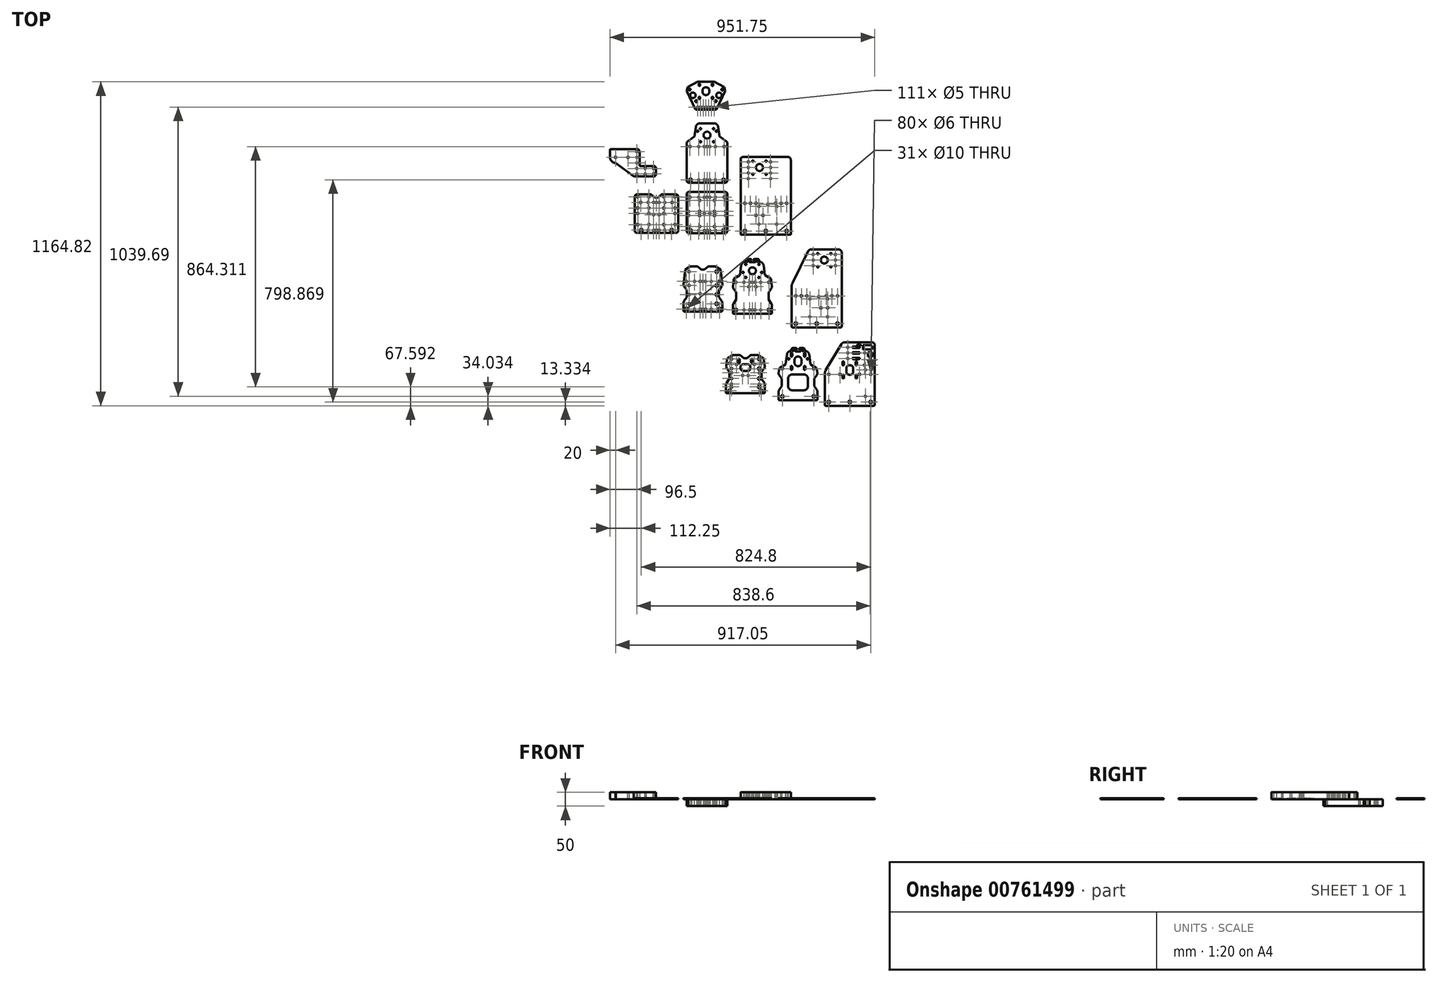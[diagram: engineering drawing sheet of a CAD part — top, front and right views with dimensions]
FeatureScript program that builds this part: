
annotation { "Feature Type Name" : "Feature", "Feature Type Description" : "" }
export const myFeature = defineFeature(function(context is Context, id is Id, definition is map)
    precondition{}
    {
        {
            var Q0;
            Q0=qCreatedBy(makeId("Top.planeOp"),FACE);
            var sketch = newSketch(context, id + "F0", { "sketchPlane" : qUnion([Q0])});
            skLineSegment(sketch, "E0", {"start": v(-86.67, -113.77) * mm, "end": v(86.64, -113.77) * mm});
            skLineSegment(sketch, "E1", {"start": v(-90, -1.46) * mm, "end": v(-90, -110.4) * mm});
            skLineSegment(sketch, "E2", {"start": v(-30.03, 107.94) * mm, "end": v(-86.68, 13.65) * mm});
            skLineSegment(sketch, "E3", {"start": v(-26.11, -13.56) * mm, "end": v(-26.11, -4.56) * mm});
            skLineSegment(sketch, "E4", {"start": v(-26.11, 33.58) * mm, "end": v(-26.11, 42.58) * mm});
            skLineSegment(sketch, "E5", {"start": v(-21.03, 42.58) * mm, "end": v(-21.03, 33.58) * mm});
            skLineSegment(sketch, "E6", {"start": v(-21.03, -4.56) * mm, "end": v(-21.03, -13.56) * mm});
            skLineSegment(sketch, "E7", {"start": v(-12.5, 9.51) * mm, "end": v(-12.5, 19.51) * mm});
            skLineSegment(sketch, "E8", {"start": v(12.5, 19.51) * mm, "end": v(12.5, 9.51) * mm});
            skLineSegment(sketch, "E9", {"start": v(21.03, -13.56) * mm, "end": v(21.03, -4.56) * mm});
            skLineSegment(sketch, "E10", {"start": v(21.03, 33.58) * mm, "end": v(21.03, 42.58) * mm});
            skLineSegment(sketch, "E11", {"start": v(26.1, 42.58) * mm, "end": v(26.1, 33.58) * mm});
            skLineSegment(sketch, "E12", {"start": v(26.1, -4.56) * mm, "end": v(26.1, -13.56) * mm});
            skLineSegment(sketch, "E13", {"start": v(27.19, 103.2) * mm, "end": v(27.19, 105.32) * mm});
            skLineSegment(sketch, "E14", {"start": v(76.37, 62.2) * mm, "end": v(75.8, 61.48) * mm});
            skLineSegment(sketch, "E15", {"start": v(39.19, 105.32) * mm, "end": v(39.19, 103.2) * mm});
            skLineSegment(sketch, "E16", {"start": v(47, 91.4) * mm, "end": v(47, 101.1) * mm});
            skLineSegment(sketch, "E17", {"start": v(33.19, 53.67) * mm, "end": v(12.19, 53.67) * mm});
            skLineSegment(sketch, "E18", {"start": v(12.19, 58.67) * mm, "end": v(33.19, 58.67) * mm});
            skLineSegment(sketch, "E19", {"start": v(65.8, 64.35) * mm, "end": v(65.8, 76.68) * mm});
            skLineSegment(sketch, "E20", {"start": v(78.84, 62.2) * mm, "end": v(76.37, 62.2) * mm});
            skLineSegment(sketch, "E21", {"start": v(69.93, 62.7) * mm, "end": v(67.46, 62.7) * mm});
            skLineSegment(sketch, "E22", {"start": v(33.19, 73.67) * mm, "end": v(12.19, 73.67) * mm});
            skLineSegment(sketch, "E23", {"start": v(67.46, 78.34) * mm, "end": v(78.84, 78.34) * mm});
            skLineSegment(sketch, "E24", {"start": v(80.5, 97.88) * mm, "end": v(80.5, 91.4) * mm});
            skLineSegment(sketch, "E25", {"start": v(80.5, 76.68) * mm, "end": v(80.5, 63.85) * mm});
            skLineSegment(sketch, "E26", {"start": v(12.19, 78.67) * mm, "end": v(33.19, 78.67) * mm});
            skLineSegment(sketch, "E27", {"start": v(77.36, 88.26) * mm, "end": v(50.14, 88.26) * mm});
            skLineSegment(sketch, "E28", {"start": v(90, -110.4) * mm, "end": v(90, 104.05) * mm});
            skLineSegment(sketch, "E29", {"start": v(33.19, 93.67) * mm, "end": v(12.19, 93.67) * mm});
            skLineSegment(sketch, "E30", {"start": v(70.9, 61.48) * mm, "end": v(69.93, 62.7) * mm});
            skLineSegment(sketch, "E31", {"start": v(12.19, 98.67) * mm, "end": v(33.19, 98.67) * mm});
            skLineSegment(sketch, "E32", {"start": v(37.75, 101.76) * mm, "end": v(28.63, 101.76) * mm});
            skLineSegment(sketch, "E33", {"start": v(50.14, 104.23) * mm, "end": v(74.15, 104.23) * mm});
            skLineSegment(sketch, "E34", {"start": v(28.63, 106.76) * mm, "end": v(37.75, 106.76) * mm});
            skLineSegment(sketch, "E35", {"start": v(80.33, 113.73) * mm, "end": v(-18.85, 113.73) * mm});
            skCircle(sketch, "E36", {"center": v(-75.3, -100.44) * mm, "radius": 5 * mm});
            skArc(sketch, "E37", {"start": v(-90, -110.4) * mm, "mid": v(-89.03, -112.77) * mm, "end": v(-86.67, -113.77) * mm});
            skArc(sketch, "E38", {"start": v(-26.11, -13.56) * mm, "mid": v(-23.57, -16.1) * mm, "end": v(-21.03, -13.56) * mm});
            skArc(sketch, "E39", {"start": v(-21.03, -4.56) * mm, "mid": v(-23.57, -2.02) * mm, "end": v(-26.11, -4.56) * mm});
            skArc(sketch, "E40", {"start": v(-86.68, 13.65) * mm, "mid": v(-89.16, 6.28) * mm, "end": v(-90, -1.46) * mm});
            skArc(sketch, "E41", {"start": v(-18.85, 113.73) * mm, "mid": v(-25.26, 112.42) * mm, "end": v(-30.03, 107.94) * mm});
            skArc(sketch, "E42", {"start": v(-21.03, 42.58) * mm, "mid": v(-23.57, 45.12) * mm, "end": v(-26.11, 42.58) * mm});
            skArc(sketch, "E43", {"start": v(-26.11, 33.58) * mm, "mid": v(-23.57, 31.04) * mm, "end": v(-21.03, 33.58) * mm});
            skCircle(sketch, "E44", {"center": v(-7.31, 96.17) * mm, "radius": 2.5 * mm});
            skCircle(sketch, "E45", {"center": v(-7.31, 76.17) * mm, "radius": 2.5 * mm});
            skCircle(sketch, "E46", {"center": v(-7.31, 56.17) * mm, "radius": 2.5 * mm});
            skCircle(sketch, "E47", {"center": v(-35.3, -0.74) * mm, "radius": 3 * mm});
            skCircle(sketch, "E48", {"center": v(-75.3, -0.74) * mm, "radius": 3 * mm});
            skCircle(sketch, "E49", {"center": v(75.3, -100.44) * mm, "radius": 5 * mm});
            skCircle(sketch, "E50", {"center": v(0, -100.44) * mm, "radius": 5 * mm});
            skArc(sketch, "E51", {"start": v(86.64, -113.77) * mm, "mid": v(89.02, -112.78) * mm, "end": v(90, -110.4) * mm});
            skArc(sketch, "E52", {"start": v(21.03, -13.56) * mm, "mid": v(23.57, -16.1) * mm, "end": v(26.1, -13.56) * mm});
            skArc(sketch, "E53", {"start": v(26.1, -4.56) * mm, "mid": v(23.57, -2.02) * mm, "end": v(21.03, -4.56) * mm});
            skCircle(sketch, "E54", {"center": v(56.34, -79.74) * mm, "radius": 2.5 * mm});
            skArc(sketch, "E55", {"start": v(-12.5, 9.51) * mm, "mid": v(0, -2.99) * mm, "end": v(12.5, 9.51) * mm});
            skArc(sketch, "E56", {"start": v(12.5, 19.51) * mm, "mid": v(0, 32.01) * mm, "end": v(-12.5, 19.51) * mm});
            skArc(sketch, "E57", {"start": v(90, 104.05) * mm, "mid": v(87.17, 110.9) * mm, "end": v(80.33, 113.73) * mm});
            skArc(sketch, "E58", {"start": v(80.5, 97.88) * mm, "mid": v(78.64, 102.37) * mm, "end": v(74.15, 104.23) * mm});
            skArc(sketch, "E59", {"start": v(77.36, 88.26) * mm, "mid": v(79.58, 89.18) * mm, "end": v(80.5, 91.4) * mm});
            skArc(sketch, "E60", {"start": v(47, 91.4) * mm, "mid": v(47.92, 89.18) * mm, "end": v(50.14, 88.26) * mm});
            skArc(sketch, "E61", {"start": v(50.14, 104.23) * mm, "mid": v(47.92, 103.31) * mm, "end": v(47, 101.1) * mm});
            skArc(sketch, "E62", {"start": v(21.03, 33.58) * mm, "mid": v(23.57, 31.04) * mm, "end": v(26.1, 33.58) * mm});
            skArc(sketch, "E63", {"start": v(26.1, 42.58) * mm, "mid": v(23.57, 45.12) * mm, "end": v(21.03, 42.58) * mm});
            skArc(sketch, "E64", {"start": v(33.19, 93.67) * mm, "mid": v(35.69, 96.17) * mm, "end": v(33.19, 98.67) * mm});
            skArc(sketch, "E65", {"start": v(12.19, 98.67) * mm, "mid": v(9.69, 96.17) * mm, "end": v(12.19, 93.67) * mm});
            skArc(sketch, "E66", {"start": v(33.19, 73.67) * mm, "mid": v(35.69, 76.17) * mm, "end": v(33.19, 78.67) * mm});
            skArc(sketch, "E67", {"start": v(12.19, 78.67) * mm, "mid": v(9.69, 76.17) * mm, "end": v(12.19, 73.67) * mm});
            skArc(sketch, "E68", {"start": v(33.19, 53.67) * mm, "mid": v(35.69, 56.17) * mm, "end": v(33.19, 58.67) * mm});
            skArc(sketch, "E69", {"start": v(12.19, 58.67) * mm, "mid": v(9.69, 56.17) * mm, "end": v(12.19, 53.67) * mm});
            skCircle(sketch, "E70", {"center": v(53.69, 76.17) * mm, "radius": 2.5 * mm});
            skCircle(sketch, "E71", {"center": v(73.35, 52.21) * mm, "radius": 2.5 * mm});
            skCircle(sketch, "E72", {"center": v(73.35, 32.21) * mm, "radius": 2.5 * mm});
            skCircle(sketch, "E73", {"center": v(52.85, 32.21) * mm, "radius": 2.5 * mm});
            skCircle(sketch, "E74", {"center": v(56.34, 15.26) * mm, "radius": 2.5 * mm});
            skCircle(sketch, "E75", {"center": v(75.3, -0.74) * mm, "radius": 3 * mm});
            skCircle(sketch, "E76", {"center": v(35.3, -0.74) * mm, "radius": 3 * mm});
            skArc(sketch, "E77", {"start": v(80.5, 76.68) * mm, "mid": v(80.01, 77.86) * mm, "end": v(78.84, 78.34) * mm});
            skArc(sketch, "E78", {"start": v(78.84, 62.2) * mm, "mid": v(80.01, 62.68) * mm, "end": v(80.5, 63.85) * mm});
            skArc(sketch, "E79", {"start": v(65.8, 64.35) * mm, "mid": v(66.29, 63.18) * mm, "end": v(67.46, 62.7) * mm});
            skArc(sketch, "E80", {"start": v(67.46, 78.34) * mm, "mid": v(66.29, 77.86) * mm, "end": v(65.8, 76.68) * mm});
            skArc(sketch, "E81", {"start": v(39.19, 105.32) * mm, "mid": v(38.77, 106.34) * mm, "end": v(37.75, 106.76) * mm});
            skArc(sketch, "E82", {"start": v(37.75, 101.76) * mm, "mid": v(38.77, 102.19) * mm, "end": v(39.19, 103.2) * mm});
            skArc(sketch, "E83", {"start": v(27.19, 103.2) * mm, "mid": v(27.61, 102.19) * mm, "end": v(28.63, 101.76) * mm});
            skArc(sketch, "E84", {"start": v(28.63, 106.76) * mm, "mid": v(27.61, 106.34) * mm, "end": v(27.19, 105.32) * mm});
            skEllipticalArc(sketch, "E85", {});
            const initialGuessF0  = {"E85": [0.07334998479999985, 0.06148353816120338, 1, 0, 0.0024529870000000007, 0.0024529870000000007, 3.141592307179585, 0]};
            skSetInitialGuess(sketch, initialGuessF0);
            skSolve(sketch);
        }
        {
            var Q0;
            Q0 = qSketchRegion(id + "F0", true);
            extrude(context, id + "F1", {"entities" : qUnion([Q0]), "depth" : 3 * mm, "offsetDistance" : 25 * mm});
        }
        {
            var Q0;
            Q0=qCreatedBy(makeId("Top.planeOp"),FACE);
            var sketch = newSketch(context, id + "F2", { "sketchPlane" : qUnion([Q0])});
            skLineSegment(sketch, "E86", {"start": v(-252.64, -93.7) * mm, "end": v(-119.36, -93.7) * mm});
            skLineSegment(sketch, "E87", {"start": v(-256, -62.59) * mm, "end": v(-256, -90.34) * mm});
            skLineSegment(sketch, "E88", {"start": v(-255.52, 3.6) * mm, "end": v(-253.3, 19.33) * mm});
            skLineSegment(sketch, "E89", {"start": v(-253.3, 19.33) * mm, "end": v(-253, 20.67) * mm});
            skLineSegment(sketch, "E90", {"start": v(-253, 20.67) * mm, "end": v(-252.46, 21.77) * mm});
            skLineSegment(sketch, "E91", {"start": v(-252.46, 21.77) * mm, "end": v(-251.76, 22.64) * mm});
            skLineSegment(sketch, "E92", {"start": v(-251.76, 22.64) * mm, "end": v(-250.88, 23.32) * mm});
            skLineSegment(sketch, "E93", {"start": v(-256, -62.59) * mm, "end": v(-255.87, -61.2) * mm});
            skLineSegment(sketch, "E94", {"start": v(-255.87, -61.2) * mm, "end": v(-255.45, -59.71) * mm});
            skLineSegment(sketch, "E95", {"start": v(-255.45, -59.71) * mm, "end": v(-254.73, -58.15) * mm});
            skLineSegment(sketch, "E96", {"start": v(-254.73, -58.15) * mm, "end": v(-253.73, -56.54) * mm});
            skLineSegment(sketch, "E97", {"start": v(-182.5, 90.85) * mm, "end": v(-180.18, 93.05) * mm});
            skLineSegment(sketch, "E98", {"start": v(-205.8, -58.65) * mm, "end": v(-166.2, -58.65) * mm});
            skLineSegment(sketch, "E99", {"start": v(-244.43, -16.42) * mm, "end": v(-252.79, -4.43) * mm});
            skLineSegment(sketch, "E100", {"start": v(-252.79, -4.43) * mm, "end": v(-253.92, -2.65) * mm});
            skLineSegment(sketch, "E101", {"start": v(-253.92, -2.65) * mm, "end": v(-254.76, -0.94) * mm});
            skLineSegment(sketch, "E102", {"start": v(-254.76, -0.94) * mm, "end": v(-255.32, 0.7) * mm});
            skLineSegment(sketch, "E103", {"start": v(-255.32, 0.7) * mm, "end": v(-255.56, 2.22) * mm});
            skLineSegment(sketch, "E104", {"start": v(-255.56, 2.22) * mm, "end": v(-255.52, 3.6) * mm});
            skLineSegment(sketch, "E105", {"start": v(-244, -41.83) * mm, "end": v(-244, -17.76) * mm});
            skLineSegment(sketch, "E106", {"start": v(-230.92, 36.33) * mm, "end": v(-226.1, 70.65) * mm});
            skLineSegment(sketch, "E107", {"start": v(-211.35, 84.55) * mm, "end": v(-210.83, 86.12) * mm});
            skLineSegment(sketch, "E108", {"start": v(-250.88, 23.32) * mm, "end": v(-232.03, 34.64) * mm});
            skLineSegment(sketch, "E109", {"start": v(-221.85, -17) * mm, "end": v(-221.85, -42.6) * mm});
            skLineSegment(sketch, "E110", {"start": v(-212.11, 73.84) * mm, "end": v(-212.11, 64.84) * mm});
            skLineSegment(sketch, "E111", {"start": v(-212.11, 26.7) * mm, "end": v(-212.11, 17.7) * mm});
            skLineSegment(sketch, "E112", {"start": v(-207.03, 17.7) * mm, "end": v(-207.03, 26.7) * mm});
            skLineSegment(sketch, "E113", {"start": v(-207.03, 64.84) * mm, "end": v(-207.03, 73.84) * mm});
            skLineSegment(sketch, "E114", {"start": v(-253.73, -56.54) * mm, "end": v(-244.43, -43.18) * mm});
            skLineSegment(sketch, "E115", {"start": v(-198.5, 50.77) * mm, "end": v(-198.5, 40.77) * mm});
            skLineSegment(sketch, "E116", {"start": v(-166.2, -0.95) * mm, "end": v(-205.8, -0.95) * mm});
            skLineSegment(sketch, "E117", {"start": v(-173.5, 40.77) * mm, "end": v(-173.5, 50.77) * mm});
            skLineSegment(sketch, "E118", {"start": v(-164.97, 73.84) * mm, "end": v(-164.97, 64.84) * mm});
            skLineSegment(sketch, "E119", {"start": v(-164.97, 26.7) * mm, "end": v(-164.97, 17.7) * mm});
            skLineSegment(sketch, "E120", {"start": v(-127.57, -43.17) * mm, "end": v(-118.27, -56.54) * mm});
            skLineSegment(sketch, "E121", {"start": v(-159.9, 17.7) * mm, "end": v(-159.9, 26.7) * mm});
            skLineSegment(sketch, "E122", {"start": v(-159.9, 64.84) * mm, "end": v(-159.9, 73.84) * mm});
            skLineSegment(sketch, "E123", {"start": v(-150.15, -42.6) * mm, "end": v(-150.15, -17) * mm});
            skLineSegment(sketch, "E124", {"start": v(-139.97, 34.64) * mm, "end": v(-121.12, 23.32) * mm});
            skLineSegment(sketch, "E125", {"start": v(-161.17, 86.12) * mm, "end": v(-160.65, 84.55) * mm});
            skLineSegment(sketch, "E126", {"start": v(-145.9, 70.65) * mm, "end": v(-141.08, 36.33) * mm});
            skLineSegment(sketch, "E127", {"start": v(-128, -17.76) * mm, "end": v(-128, -41.83) * mm});
            skLineSegment(sketch, "E128", {"start": v(-119.22, -4.43) * mm, "end": v(-127.57, -16.42) * mm});
            skLineSegment(sketch, "E129", {"start": v(-121.12, 23.32) * mm, "end": v(-120.22, 22.62) * mm});
            skLineSegment(sketch, "E130", {"start": v(-120.22, 22.62) * mm, "end": v(-119.51, 21.74) * mm});
            skLineSegment(sketch, "E131", {"start": v(-119.51, 21.74) * mm, "end": v(-119, 20.65) * mm});
            skLineSegment(sketch, "E132", {"start": v(-119, 20.65) * mm, "end": v(-118.7, 19.33) * mm});
            skLineSegment(sketch, "E133", {"start": v(-191.82, 93.05) * mm, "end": v(-189.5, 90.85) * mm});
            skLineSegment(sketch, "E134", {"start": v(-116, -62.59) * mm, "end": v(-116.13, -61.2) * mm});
            skLineSegment(sketch, "E135", {"start": v(-116.13, -61.2) * mm, "end": v(-116.55, -59.71) * mm});
            skLineSegment(sketch, "E136", {"start": v(-116.55, -59.71) * mm, "end": v(-117.27, -58.15) * mm});
            skLineSegment(sketch, "E137", {"start": v(-117.27, -58.15) * mm, "end": v(-118.27, -56.54) * mm});
            skLineSegment(sketch, "E138", {"start": v(-118.7, 19.33) * mm, "end": v(-116.48, 3.6) * mm});
            skLineSegment(sketch, "E139", {"start": v(-116.48, 3.6) * mm, "end": v(-116.43, 2.22) * mm});
            skLineSegment(sketch, "E140", {"start": v(-116.43, 2.22) * mm, "end": v(-116.68, 0.7) * mm});
            skLineSegment(sketch, "E141", {"start": v(-116.68, 0.7) * mm, "end": v(-117.24, -0.94) * mm});
            skLineSegment(sketch, "E142", {"start": v(-117.24, -0.94) * mm, "end": v(-118.09, -2.65) * mm});
            skLineSegment(sketch, "E143", {"start": v(-118.09, -2.65) * mm, "end": v(-119.22, -4.43) * mm});
            skLineSegment(sketch, "E144", {"start": v(-116, -90.34) * mm, "end": v(-116, -62.59) * mm});
            skLineSegment(sketch, "E145", {"start": v(-193.5, 81.5) * mm, "end": v(-178.5, 81.5) * mm});
            skLineSegment(sketch, "E146", {"start": v(-178.5, 89.5) * mm, "end": v(-181.15, 89.5) * mm});
            skLineSegment(sketch, "E147", {"start": v(-190.85, 89.5) * mm, "end": v(-193.5, 89.5) * mm});
            skLineSegment(sketch, "E148", {"start": v(-168.09, 93.7) * mm, "end": v(-178.56, 93.7) * mm});
            skLineSegment(sketch, "E149", {"start": v(-193.44, 93.7) * mm, "end": v(-203.91, 93.7) * mm});
            skArc(sketch, "E150", {"start": v(-205.8, -0.95) * mm, "mid": v(-217.15, -5.65) * mm, "end": v(-221.85, -17) * mm});
            skArc(sketch, "E151", {"start": v(-221.85, -42.6) * mm, "mid": v(-217.15, -53.95) * mm, "end": v(-205.8, -58.65) * mm});
            skCircle(sketch, "E152", {"center": v(-242.5, -80.18) * mm, "radius": 5 * mm});
            skArc(sketch, "E153", {"start": v(-256, -90.34) * mm, "mid": v(-255.02, -92.72) * mm, "end": v(-252.64, -93.7) * mm});
            skArc(sketch, "E154", {"start": v(-244, -17.76) * mm, "mid": v(-244.11, -17.06) * mm, "end": v(-244.43, -16.42) * mm});
            skArc(sketch, "E155", {"start": v(-244.43, -43.18) * mm, "mid": v(-244.11, -42.54) * mm, "end": v(-244, -41.83) * mm});
            skArc(sketch, "E156", {"start": v(-213.34, 82.95) * mm, "mid": v(-221.84, 79) * mm, "end": v(-226.1, 70.65) * mm});
            skArc(sketch, "E157", {"start": v(-203.91, 93.7) * mm, "mid": v(-208.37, 91.91) * mm, "end": v(-210.36, 87.54) * mm});
            skArc(sketch, "E158", {"start": v(-193.5, 89.5) * mm, "mid": v(-197.5, 85.5) * mm, "end": v(-193.5, 81.5) * mm});
            skCircle(sketch, "E159", {"center": v(-203.9, 85.5) * mm, "radius": 2.73 * mm});
            skCircle(sketch, "E160", {"center": v(-219.8, 54.95) * mm, "radius": 2.73 * mm});
            skArc(sketch, "E161", {"start": v(-207.03, 73.84) * mm, "mid": v(-209.57, 76.38) * mm, "end": v(-212.11, 73.84) * mm});
            skArc(sketch, "E162", {"start": v(-212.11, 64.84) * mm, "mid": v(-209.57, 62.3) * mm, "end": v(-207.03, 64.84) * mm});
            skArc(sketch, "E163", {"start": v(-207.03, 26.7) * mm, "mid": v(-209.57, 29.24) * mm, "end": v(-212.11, 26.7) * mm});
            skArc(sketch, "E164", {"start": v(-212.11, 17.7) * mm, "mid": v(-209.57, 15.16) * mm, "end": v(-207.03, 17.7) * mm});
            skCircle(sketch, "E165", {"center": v(-242.5, 19.52) * mm, "radius": 3 * mm});
            skArc(sketch, "E166", {"start": v(-232.03, 34.64) * mm, "mid": v(-231.29, 35.36) * mm, "end": v(-230.92, 36.33) * mm});
            skArc(sketch, "E167", {"start": v(-213.34, 82.95) * mm, "mid": v(-212.1, 83.46) * mm, "end": v(-211.35, 84.55) * mm});
            skArc(sketch, "E168", {"start": v(-191.82, 93.05) * mm, "mid": v(-192.57, 93.53) * mm, "end": v(-193.44, 93.7) * mm});
            skArc(sketch, "E169", {"start": v(-190.85, 89.5) * mm, "mid": v(-189.47, 89.47) * mm, "end": v(-189.5, 90.85) * mm});
            skArc(sketch, "E170", {"start": v(-210.83, 86.12) * mm, "mid": v(-210.12, 86.67) * mm, "end": v(-210.36, 87.54) * mm});
            skArc(sketch, "E171", {"start": v(-166.2, -58.65) * mm, "mid": v(-154.85, -53.95) * mm, "end": v(-150.15, -42.6) * mm});
            skArc(sketch, "E172", {"start": v(-150.15, -17) * mm, "mid": v(-154.85, -5.65) * mm, "end": v(-166.2, -0.95) * mm});
            skCircle(sketch, "E173", {"center": v(-129.5, -80.18) * mm, "radius": 5 * mm});
            skArc(sketch, "E174", {"start": v(-119.36, -93.7) * mm, "mid": v(-116.98, -92.72) * mm, "end": v(-116, -90.34) * mm});
            skArc(sketch, "E175", {"start": v(-127.57, -16.42) * mm, "mid": v(-127.88, -17.06) * mm, "end": v(-128, -17.76) * mm});
            skArc(sketch, "E176", {"start": v(-128, -41.83) * mm, "mid": v(-127.88, -42.54) * mm, "end": v(-127.57, -43.17) * mm});
            skArc(sketch, "E177", {"start": v(-145.9, 70.65) * mm, "mid": v(-150.16, 79) * mm, "end": v(-158.66, 82.95) * mm});
            skArc(sketch, "E178", {"start": v(-173.5, 50.77) * mm, "mid": v(-186, 63.27) * mm, "end": v(-198.5, 50.77) * mm});
            skArc(sketch, "E179", {"start": v(-198.5, 40.77) * mm, "mid": v(-186, 28.27) * mm, "end": v(-173.5, 40.77) * mm});
            skArc(sketch, "E180", {"start": v(-161.64, 87.54) * mm, "mid": v(-163.63, 91.91) * mm, "end": v(-168.09, 93.7) * mm});
            skArc(sketch, "E181", {"start": v(-178.5, 81.5) * mm, "mid": v(-174.5, 85.5) * mm, "end": v(-178.5, 89.5) * mm});
            skCircle(sketch, "E182", {"center": v(-168.1, 85.5) * mm, "radius": 2.73 * mm});
            skCircle(sketch, "E183", {"center": v(-152.2, 54.95) * mm, "radius": 2.73 * mm});
            skArc(sketch, "E184", {"start": v(-159.9, 73.84) * mm, "mid": v(-162.43, 76.38) * mm, "end": v(-164.97, 73.84) * mm});
            skArc(sketch, "E185", {"start": v(-164.97, 64.84) * mm, "mid": v(-162.43, 62.3) * mm, "end": v(-159.9, 64.84) * mm});
            skArc(sketch, "E186", {"start": v(-159.9, 26.7) * mm, "mid": v(-162.43, 29.24) * mm, "end": v(-164.97, 26.7) * mm});
            skArc(sketch, "E187", {"start": v(-164.97, 17.7) * mm, "mid": v(-162.43, 15.16) * mm, "end": v(-159.9, 17.7) * mm});
            skCircle(sketch, "E188", {"center": v(-129.5, 19.52) * mm, "radius": 3 * mm});
            skArc(sketch, "E189", {"start": v(-141.08, 36.33) * mm, "mid": v(-140.71, 35.36) * mm, "end": v(-139.97, 34.64) * mm});
            skArc(sketch, "E190", {"start": v(-160.65, 84.55) * mm, "mid": v(-159.9, 83.46) * mm, "end": v(-158.66, 82.95) * mm});
            skArc(sketch, "E191", {"start": v(-178.56, 93.7) * mm, "mid": v(-179.43, 93.53) * mm, "end": v(-180.18, 93.05) * mm});
            skArc(sketch, "E192", {"start": v(-182.5, 90.85) * mm, "mid": v(-182.53, 89.47) * mm, "end": v(-181.15, 89.5) * mm});
            skArc(sketch, "E193", {"start": v(-161.64, 87.54) * mm, "mid": v(-161.88, 86.67) * mm, "end": v(-161.17, 86.12) * mm});
            skSolve(sketch);
        }
        {
            var Q0;
            Q0=qCreatedBy(makeId("Top.planeOp"),FACE);
            var sketch = newSketch(context, id + "F3", { "sketchPlane" : qUnion([Q0])});
            skLineSegment(sketch, "E194", {"start": v(-438.59, 57.34) * mm, "end": v(-439.5, 56.65) * mm});
            skLineSegment(sketch, "E195", {"start": v(-439.5, 56.65) * mm, "end": v(-440.2, 55.76) * mm});
            skLineSegment(sketch, "E196", {"start": v(-440.2, 55.76) * mm, "end": v(-440.7, 54.68) * mm});
            skLineSegment(sketch, "E197", {"start": v(-440.7, 54.68) * mm, "end": v(-441.02, 53.35) * mm});
            skLineSegment(sketch, "E198", {"start": v(-438.59, 57.34) * mm, "end": v(-420.13, 68.52) * mm});
            skLineSegment(sketch, "E199", {"start": v(-445, -37.75) * mm, "end": v(-445, -65.5) * mm});
            skLineSegment(sketch, "E200", {"start": v(-444.52, 28.45) * mm, "end": v(-441.02, 53.35) * mm});
            skLineSegment(sketch, "E201", {"start": v(-445, -37.75) * mm, "end": v(-444.87, -36.37) * mm});
            skLineSegment(sketch, "E202", {"start": v(-444.87, -36.37) * mm, "end": v(-444.45, -34.88) * mm});
            skLineSegment(sketch, "E203", {"start": v(-444.45, -34.88) * mm, "end": v(-443.74, -33.32) * mm});
            skLineSegment(sketch, "E204", {"start": v(-443.74, -33.32) * mm, "end": v(-442.73, -31.7) * mm});
            skLineSegment(sketch, "E205", {"start": v(-441.64, -68.86) * mm, "end": v(-395.35, -68.86) * mm});
            skLineSegment(sketch, "E206", {"start": v(-354.65, -68.86) * mm, "end": v(-308.36, -68.86) * mm});
            skLineSegment(sketch, "E207", {"start": v(-433, -17) * mm, "end": v(-433, 7.08) * mm});
            skLineSegment(sketch, "E208", {"start": v(-433.43, 8.42) * mm, "end": v(-441.79, 20.4) * mm});
            skLineSegment(sketch, "E209", {"start": v(-441.79, 20.4) * mm, "end": v(-442.92, 22.2) * mm});
            skLineSegment(sketch, "E210", {"start": v(-442.92, 22.2) * mm, "end": v(-443.77, 23.92) * mm});
            skLineSegment(sketch, "E211", {"start": v(-443.77, 23.92) * mm, "end": v(-444.32, 25.55) * mm});
            skLineSegment(sketch, "E212", {"start": v(-444.32, 25.55) * mm, "end": v(-444.57, 27.07) * mm});
            skLineSegment(sketch, "E213", {"start": v(-444.57, 27.07) * mm, "end": v(-444.52, 28.45) * mm});
            skLineSegment(sketch, "E214", {"start": v(-442.73, -31.7) * mm, "end": v(-433.43, -18.34) * mm});
            skLineSegment(sketch, "E215", {"start": v(-369.34, 57.25) * mm, "end": v(-356.16, 68.31) * mm});
            skLineSegment(sketch, "E216", {"start": v(-401.57, 51.54) * mm, "end": v(-401.57, 42.54) * mm});
            skLineSegment(sketch, "E217", {"start": v(-395.57, 42.54) * mm, "end": v(-395.57, 51.54) * mm});
            skLineSegment(sketch, "E218", {"start": v(-392.5, 26.1) * mm, "end": v(-392.5, 20.2) * mm});
            skLineSegment(sketch, "E219", {"start": v(-383.45, 11.15) * mm, "end": v(-366.55, 11.15) * mm});
            skLineSegment(sketch, "E220", {"start": v(-357.5, 20.2) * mm, "end": v(-357.5, 26.1) * mm});
            skLineSegment(sketch, "E221", {"start": v(-354.43, 51.54) * mm, "end": v(-354.43, 42.54) * mm});
            skLineSegment(sketch, "E222", {"start": v(-348.43, 42.54) * mm, "end": v(-348.43, 51.54) * mm});
            skLineSegment(sketch, "E223", {"start": v(-366.55, 35.15) * mm, "end": v(-383.45, 35.15) * mm});
            skLineSegment(sketch, "E224", {"start": v(-393.84, 68.31) * mm, "end": v(-380.66, 57.25) * mm});
            skLineSegment(sketch, "E225", {"start": v(-316.57, -18.33) * mm, "end": v(-307.27, -31.7) * mm});
            skLineSegment(sketch, "E226", {"start": v(-308.22, 20.4) * mm, "end": v(-316.57, 8.42) * mm});
            skLineSegment(sketch, "E227", {"start": v(-379.14, 56.7) * mm, "end": v(-370.86, 56.7) * mm});
            skLineSegment(sketch, "E228", {"start": v(-316.99, 7.08) * mm, "end": v(-316.99, -17) * mm});
            skLineSegment(sketch, "E229", {"start": v(-331.09, 68.86) * mm, "end": v(-354.65, 68.86) * mm});
            skLineSegment(sketch, "E230", {"start": v(-395.35, 68.86) * mm, "end": v(-418.91, 68.86) * mm});
            skLineSegment(sketch, "E231", {"start": v(-305, -37.75) * mm, "end": v(-305.13, -36.37) * mm});
            skLineSegment(sketch, "E232", {"start": v(-305.13, -36.37) * mm, "end": v(-305.55, -34.88) * mm});
            skLineSegment(sketch, "E233", {"start": v(-305.55, -34.88) * mm, "end": v(-306.26, -33.32) * mm});
            skLineSegment(sketch, "E234", {"start": v(-306.26, -33.32) * mm, "end": v(-307.27, -31.7) * mm});
            skLineSegment(sketch, "E235", {"start": v(-305.48, 28.45) * mm, "end": v(-305.43, 27.07) * mm});
            skLineSegment(sketch, "E236", {"start": v(-305.43, 27.07) * mm, "end": v(-305.68, 25.55) * mm});
            skLineSegment(sketch, "E237", {"start": v(-305.68, 25.55) * mm, "end": v(-306.23, 23.92) * mm});
            skLineSegment(sketch, "E238", {"start": v(-306.23, 23.92) * mm, "end": v(-307.08, 22.2) * mm});
            skLineSegment(sketch, "E239", {"start": v(-307.08, 22.2) * mm, "end": v(-308.22, 20.4) * mm});
            skLineSegment(sketch, "E240", {"start": v(-305, -65.5) * mm, "end": v(-305, -37.75) * mm});
            skLineSegment(sketch, "E241", {"start": v(-308.98, 53.35) * mm, "end": v(-309.3, 54.7) * mm});
            skLineSegment(sketch, "E242", {"start": v(-309.3, 54.7) * mm, "end": v(-309.83, 55.8) * mm});
            skLineSegment(sketch, "E243", {"start": v(-309.83, 55.8) * mm, "end": v(-310.53, 56.66) * mm});
            skLineSegment(sketch, "E244", {"start": v(-310.53, 56.66) * mm, "end": v(-311.41, 57.34) * mm});
            skLineSegment(sketch, "E245", {"start": v(-308.98, 53.35) * mm, "end": v(-305.48, 28.45) * mm});
            skLineSegment(sketch, "E246", {"start": v(-329.87, 68.52) * mm, "end": v(-311.41, 57.34) * mm});
            skCircle(sketch, "E247", {"center": v(-431.5, -60.34) * mm, "radius": 5 * mm});
            skArc(sketch, "E248", {"start": v(-445, -65.5) * mm, "mid": v(-444.02, -67.88) * mm, "end": v(-441.64, -68.86) * mm});
            skCircle(sketch, "E249", {"center": v(-385, -4.96) * mm, "radius": 2.5 * mm});
            skCircle(sketch, "E250", {"center": v(-424.85, -46.18) * mm, "radius": 3 * mm});
            skCircle(sketch, "E251", {"center": v(-424.85, -36.18) * mm, "radius": 2.5 * mm});
            skCircle(sketch, "E252", {"center": v(-424.85, -15.86) * mm, "radius": 3 * mm});
            skCircle(sketch, "E253", {"center": v(-424.85, 4.46) * mm, "radius": 2.5 * mm});
            skArc(sketch, "E254", {"start": v(-433.43, -18.34) * mm, "mid": v(-433.11, -17.7) * mm, "end": v(-433, -17) * mm});
            skArc(sketch, "E255", {"start": v(-383.45, 35.15) * mm, "mid": v(-389.85, 32.5) * mm, "end": v(-392.5, 26.1) * mm});
            skArc(sketch, "E256", {"start": v(-392.5, 20.2) * mm, "mid": v(-389.85, 13.8) * mm, "end": v(-383.45, 11.15) * mm});
            skArc(sketch, "E257", {"start": v(-395.57, 51.54) * mm, "mid": v(-398.57, 54.54) * mm, "end": v(-401.57, 51.54) * mm});
            skArc(sketch, "E258", {"start": v(-401.57, 42.54) * mm, "mid": v(-398.57, 39.54) * mm, "end": v(-395.57, 42.54) * mm});
            skCircle(sketch, "E259", {"center": v(-406.92, 34.36) * mm, "radius": 2.5 * mm});
            skCircle(sketch, "E260", {"center": v(-424.85, 19.46) * mm, "radius": 3 * mm});
            skCircle(sketch, "E261", {"center": v(-424.85, 54.46) * mm, "radius": 3 * mm});
            skCircle(sketch, "E262", {"center": v(-431.5, 39.36) * mm, "radius": 3 * mm});
            skArc(sketch, "E263", {"start": v(-433, 7.08) * mm, "mid": v(-433.11, 7.78) * mm, "end": v(-433.43, 8.42) * mm});
            skArc(sketch, "E264", {"start": v(-380.66, 57.25) * mm, "mid": v(-379.95, 56.84) * mm, "end": v(-379.14, 56.7) * mm});
            skArc(sketch, "E265", {"start": v(-393.84, 68.31) * mm, "mid": v(-394.54, 68.72) * mm, "end": v(-395.35, 68.86) * mm});
            skArc(sketch, "E266", {"start": v(-418.91, 68.86) * mm, "mid": v(-419.54, 68.77) * mm, "end": v(-420.13, 68.52) * mm});
            skCircle(sketch, "E267", {"center": v(-325.15, -46.18) * mm, "radius": 5 * mm});
            skCircle(sketch, "E268", {"center": v(-325.15, -15.86) * mm, "radius": 5 * mm});
            skCircle(sketch, "E269", {"center": v(-318.5, -60.34) * mm, "radius": 5 * mm});
            skArc(sketch, "E270", {"start": v(-308.36, -68.86) * mm, "mid": v(-305.98, -67.88) * mm, "end": v(-305, -65.5) * mm});
            skCircle(sketch, "E271", {"center": v(-365, -4.96) * mm, "radius": 2.5 * mm});
            skCircle(sketch, "E272", {"center": v(-325.15, -36.18) * mm, "radius": 2.5 * mm});
            skCircle(sketch, "E273", {"center": v(-325.15, 4.46) * mm, "radius": 2.5 * mm});
            skArc(sketch, "E274", {"start": v(-316.99, -17) * mm, "mid": v(-316.88, -17.7) * mm, "end": v(-316.57, -18.33) * mm});
            skArc(sketch, "E275", {"start": v(-366.55, 11.15) * mm, "mid": v(-360.15, 13.8) * mm, "end": v(-357.5, 20.2) * mm});
            skArc(sketch, "E276", {"start": v(-357.5, 26.1) * mm, "mid": v(-360.15, 32.5) * mm, "end": v(-366.55, 35.15) * mm});
            skCircle(sketch, "E277", {"center": v(-325.15, 19.46) * mm, "radius": 5 * mm});
            skCircle(sketch, "E278", {"center": v(-325.15, 54.46) * mm, "radius": 5 * mm});
            skArc(sketch, "E279", {"start": v(-348.43, 51.54) * mm, "mid": v(-351.43, 54.54) * mm, "end": v(-354.43, 51.54) * mm});
            skArc(sketch, "E280", {"start": v(-354.43, 42.54) * mm, "mid": v(-351.43, 39.54) * mm, "end": v(-348.43, 42.54) * mm});
            skCircle(sketch, "E281", {"center": v(-343.07, 34.36) * mm, "radius": 2.5 * mm});
            skCircle(sketch, "E282", {"center": v(-318.5, 39.36) * mm, "radius": 3 * mm});
            skArc(sketch, "E283", {"start": v(-316.57, 8.42) * mm, "mid": v(-316.88, 7.78) * mm, "end": v(-316.99, 7.08) * mm});
            skArc(sketch, "E284", {"start": v(-370.86, 56.7) * mm, "mid": v(-370.05, 56.84) * mm, "end": v(-369.34, 57.25) * mm});
            skArc(sketch, "E285", {"start": v(-354.65, 68.86) * mm, "mid": v(-355.46, 68.72) * mm, "end": v(-356.16, 68.31) * mm});
            skArc(sketch, "E286", {"start": v(-329.87, 68.52) * mm, "mid": v(-330.46, 68.77) * mm, "end": v(-331.09, 68.86) * mm});
            skLineSegment(sketch, "E287", {"start": v(-395.35, -68.86) * mm, "end": v(-354.65, -68.86) * mm});
            skSolve(sketch);
        }
        {
            var Q0;
            Q0=makeQuery(id+"F3.imprint","IMPRINT",FACE,{"disambiguationData":[TD([[makeQuery(id+"F3.imprint","IMPRINT",EDGE,{"derivedFrom":sQuery(id+"F3.wireOp",EDGE,"E194")}),1.0]])]});
            extrude(context, id + "F4", {"entities" : qUnion([Q0]), "depth" : 3 * mm, "offsetDistance" : 25 * mm});
        }
        {
            var Q0;
            Q0=makeQuery(id+"F2.imprint","IMPRINT",FACE,{"disambiguationData":[TD([[makeQuery(id+"F2.imprint","IMPRINT",EDGE,{"derivedFrom":sQuery(id+"F2.wireOp",EDGE,"E86")}),1.0]])]});
            extrude(context, id + "F5", {"entities" : qUnion([Q0]), "depth" : 3 * mm, "offsetDistance" : 25 * mm});
        }
        {
            var Q0;
            Q0=qCreatedBy(makeId("Top.planeOp"),FACE);
            var sketch = newSketch(context, id + "F6", { "sketchPlane" : qUnion([Q0])});
            skCircle(sketch, "E288", {"center": v(-44, 181.5) * mm, "radius": 5 * mm});
            skCircle(sketch, "E289", {"center": v(-119, 181.5) * mm, "radius": 5 * mm});
            skCircle(sketch, "E290", {"center": v(-194, 181.5) * mm, "radius": 5 * mm});
            skCircle(sketch, "E291", {"center": v(-44, 281.2) * mm, "radius": 3 * mm});
            skCircle(sketch, "E292", {"center": v(-84, 281.2) * mm, "radius": 3 * mm});
            skCircle(sketch, "E293", {"center": v(-154, 281.2) * mm, "radius": 3 * mm});
            skCircle(sketch, "E294", {"center": v(-194, 281.2) * mm, "radius": 3 * mm});
            skArc(sketch, "E295", {"start": v(-204.8, 329.3) * mm, "mid": v(-207.93, 321.93) * mm, "end": v(-209, 314) * mm});
            skLineSegment(sketch, "E296", {"start": v(-149.46, 442.61) * mm, "end": v(-204.8, 329.3) * mm});
            skArc(sketch, "E297", {"start": v(-140, 448) * mm, "mid": v(-145.44, 446.56) * mm, "end": v(-149.46, 442.61) * mm});
            skLineSegment(sketch, "E298", {"start": v(-40, 448) * mm, "end": v(-140, 448) * mm});
            skArc(sketch, "E299", {"start": v(-29, 437) * mm, "mid": v(-32.22, 444.78) * mm, "end": v(-40, 448) * mm});
            skLineSegment(sketch, "E300", {"start": v(-29, 171) * mm, "end": v(-29, 437) * mm});
            skArc(sketch, "E301", {"start": v(-32, 168) * mm, "mid": v(-29.88, 168.88) * mm, "end": v(-29, 171) * mm});
            skLineSegment(sketch, "E302", {"start": v(-206, 168) * mm, "end": v(-32, 168) * mm});
            skArc(sketch, "E303", {"start": v(-209, 171) * mm, "mid": v(-208.12, 168.88) * mm, "end": v(-206, 168) * mm});
            skLineSegment(sketch, "E304", {"start": v(-209, 314) * mm, "end": v(-209, 171) * mm});
            skCircle(sketch, "E305", {"center": v(-115.07, 385.93) * mm, "radius": 2.54 * mm});
            skCircle(sketch, "E306", {"center": v(-115.07, 433.07) * mm, "radius": 2.54 * mm});
            skCircle(sketch, "E307", {"center": v(-91.5, 410) * mm, "radius": 12.5 * mm});
            skCircle(sketch, "E308", {"center": v(-67.93, 433.07) * mm, "radius": 2.54 * mm});
            skCircle(sketch, "E309", {"center": v(-67.93, 385.93) * mm, "radius": 2.54 * mm});
            skCircle(sketch, "E310", {"center": v(-131.5, 430) * mm, "radius": 2.5 * mm});
            skCircle(sketch, "E311", {"center": v(-131.5, 410) * mm, "radius": 2.5 * mm});
            skCircle(sketch, "E312", {"center": v(-131.5, 390) * mm, "radius": 2.5 * mm});
            skCircle(sketch, "E313", {"center": v(-51.5, 430) * mm, "radius": 2.5 * mm});
            skCircle(sketch, "E314", {"center": v(-51.5, 410) * mm, "radius": 2.5 * mm});
            skCircle(sketch, "E315", {"center": v(-51.5, 390) * mm, "radius": 2.5 * mm});
            skCircle(sketch, "E316", {"center": v(-174, 281.2) * mm, "radius": 3 * mm});
            skCircle(sketch, "E317", {"center": v(-64, 281.2) * mm, "radius": 3 * mm});
            skCircle(sketch, "E318", {"center": v(-104, 238.07) * mm, "radius": 3 * mm});
            skCircle(sketch, "E319", {"center": v(-79, 238.07) * mm, "radius": 3 * mm});
            skCircle(sketch, "E320", {"center": v(-111.5, 278.07) * mm, "radius": 3 * mm});
            skCircle(sketch, "E321", {"center": v(-79.5, 270.07) * mm, "radius": 2.5 * mm});
            skCircle(sketch, "E322", {"center": v(-143.5, 270.07) * mm, "radius": 2.5 * mm});
            skCircle(sketch, "E323", {"center": v(-143.5, 206.07) * mm, "radius": 2.5 * mm});
            skCircle(sketch, "E324", {"center": v(-79.5, 206.07) * mm, "radius": 2.5 * mm});
            skSolve(sketch);
        }
        {
            var Q0;
            Q0 = qSketchRegion(id + "F6", true);
            extrude(context, id + "F7", {"entities" : qUnion([Q0]), "depth" : 3 * mm, "offsetDistance" : 25 * mm});
        }
        {
            var Q0;
            Q0=qCreatedBy(makeId("Top.planeOp"),FACE);
            var sketch = newSketch(context, id + "F8", { "sketchPlane" : qUnion([Q0])});
            skLineSegment(sketch, "E325", {"start": v(-416.64, 217) * mm, "end": v(-283.36, 217) * mm});
            skLineSegment(sketch, "E326", {"start": v(-420, 248.11) * mm, "end": v(-420, 220.36) * mm});
            skLineSegment(sketch, "E327", {"start": v(-419.52, 314.3) * mm, "end": v(-417.3, 340.03) * mm});
            skLineSegment(sketch, "E328", {"start": v(-417.3, 340.03) * mm, "end": v(-417, 341.37) * mm});
            skLineSegment(sketch, "E329", {"start": v(-417, 341.37) * mm, "end": v(-416.46, 342.47) * mm});
            skLineSegment(sketch, "E330", {"start": v(-416.46, 342.47) * mm, "end": v(-415.76, 343.34) * mm});
            skLineSegment(sketch, "E331", {"start": v(-420, 248.11) * mm, "end": v(-419.87, 249.5) * mm});
            skLineSegment(sketch, "E332", {"start": v(-419.87, 249.5) * mm, "end": v(-419.45, 250.99) * mm});
            skLineSegment(sketch, "E333", {"start": v(-419.45, 250.99) * mm, "end": v(-418.73, 252.55) * mm});
            skLineSegment(sketch, "E334", {"start": v(-418.73, 252.55) * mm, "end": v(-417.73, 254.16) * mm});
            skLineSegment(sketch, "E335", {"start": v(-346.5, 411.55) * mm, "end": v(-344.18, 413.75) * mm});
            skLineSegment(sketch, "E336", {"start": v(-408.43, 294.28) * mm, "end": v(-416.79, 306.27) * mm});
            skLineSegment(sketch, "E337", {"start": v(-416.79, 306.27) * mm, "end": v(-417.92, 308.05) * mm});
            skLineSegment(sketch, "E338", {"start": v(-417.92, 308.05) * mm, "end": v(-418.76, 309.76) * mm});
            skLineSegment(sketch, "E339", {"start": v(-418.76, 309.76) * mm, "end": v(-419.32, 311.4) * mm});
            skLineSegment(sketch, "E340", {"start": v(-419.32, 311.4) * mm, "end": v(-419.56, 312.92) * mm});
            skLineSegment(sketch, "E341", {"start": v(-419.56, 312.92) * mm, "end": v(-419.52, 314.3) * mm});
            skLineSegment(sketch, "E342", {"start": v(-408, 268.87) * mm, "end": v(-408, 292.94) * mm});
            skLineSegment(sketch, "E343", {"start": v(-394.92, 357.03) * mm, "end": v(-390.1, 391.35) * mm});
            skLineSegment(sketch, "E344", {"start": v(-375.35, 405.25) * mm, "end": v(-374.83, 406.82) * mm});
            skLineSegment(sketch, "E345", {"start": v(-414.88, 344.02) * mm, "end": v(-396.03, 355.34) * mm});
            skLineSegment(sketch, "E346", {"start": v(-417.73, 254.16) * mm, "end": v(-408.43, 267.52) * mm});
            skLineSegment(sketch, "E347", {"start": v(-291.57, 267.53) * mm, "end": v(-282.27, 254.16) * mm});
            skLineSegment(sketch, "E348", {"start": v(-303.97, 355.34) * mm, "end": v(-285.12, 344.02) * mm});
            skLineSegment(sketch, "E349", {"start": v(-325.17, 406.82) * mm, "end": v(-324.65, 405.25) * mm});
            skLineSegment(sketch, "E350", {"start": v(-309.9, 391.35) * mm, "end": v(-305.08, 357.03) * mm});
            skLineSegment(sketch, "E351", {"start": v(-291.99, 292.94) * mm, "end": v(-291.99, 268.87) * mm});
            skLineSegment(sketch, "E352", {"start": v(-283.22, 306.27) * mm, "end": v(-291.57, 294.28) * mm});
            skLineSegment(sketch, "E353", {"start": v(-285.12, 344.02) * mm, "end": v(-284.22, 343.32) * mm});
            skLineSegment(sketch, "E354", {"start": v(-284.22, 343.32) * mm, "end": v(-283.51, 342.44) * mm});
            skLineSegment(sketch, "E355", {"start": v(-283.51, 342.44) * mm, "end": v(-283, 341.35) * mm});
            skLineSegment(sketch, "E356", {"start": v(-283, 341.35) * mm, "end": v(-282.7, 340.03) * mm});
            skLineSegment(sketch, "E357", {"start": v(-355.82, 413.75) * mm, "end": v(-353.5, 411.55) * mm});
            skLineSegment(sketch, "E358", {"start": v(-280, 248.11) * mm, "end": v(-280.13, 249.5) * mm});
            skLineSegment(sketch, "E359", {"start": v(-280.13, 249.5) * mm, "end": v(-280.55, 250.99) * mm});
            skLineSegment(sketch, "E360", {"start": v(-280.55, 250.99) * mm, "end": v(-281.27, 252.55) * mm});
            skLineSegment(sketch, "E361", {"start": v(-281.27, 252.55) * mm, "end": v(-282.27, 254.16) * mm});
            skLineSegment(sketch, "E362", {"start": v(-282.7, 340.03) * mm, "end": v(-280.48, 314.3) * mm});
            skLineSegment(sketch, "E363", {"start": v(-280.48, 314.3) * mm, "end": v(-280.43, 312.92) * mm});
            skLineSegment(sketch, "E364", {"start": v(-280.43, 312.92) * mm, "end": v(-280.68, 311.4) * mm});
            skLineSegment(sketch, "E365", {"start": v(-280.68, 311.4) * mm, "end": v(-281.24, 309.76) * mm});
            skLineSegment(sketch, "E366", {"start": v(-281.24, 309.76) * mm, "end": v(-282.09, 308.05) * mm});
            skLineSegment(sketch, "E367", {"start": v(-282.09, 308.05) * mm, "end": v(-283.22, 306.27) * mm});
            skLineSegment(sketch, "E368", {"start": v(-280, 220.36) * mm, "end": v(-280, 248.11) * mm});
            skLineSegment(sketch, "E369", {"start": v(-357.5, 402.2) * mm, "end": v(-342.5, 402.2) * mm});
            skLineSegment(sketch, "E370", {"start": v(-342.5, 410.2) * mm, "end": v(-345.15, 410.2) * mm});
            skLineSegment(sketch, "E371", {"start": v(-354.85, 410.2) * mm, "end": v(-357.5, 410.2) * mm});
            skLineSegment(sketch, "E372", {"start": v(-332.09, 414.4) * mm, "end": v(-342.56, 414.4) * mm});
            skLineSegment(sketch, "E373", {"start": v(-357.44, 414.4) * mm, "end": v(-367.91, 414.4) * mm});
            skCircle(sketch, "E374", {"center": v(-409.5, 230.52) * mm, "radius": 5 * mm});
            skArc(sketch, "E375", {"start": v(-420, 220.36) * mm, "mid": v(-419.02, 217.98) * mm, "end": v(-416.64, 217) * mm});
            skArc(sketch, "E376", {"start": v(-408, 292.94) * mm, "mid": v(-408.11, 293.64) * mm, "end": v(-408.43, 294.28) * mm});
            skArc(sketch, "E377", {"start": v(-408.43, 267.52) * mm, "mid": v(-408.11, 268.16) * mm, "end": v(-408, 268.87) * mm});
            skArc(sketch, "E378", {"start": v(-377.34, 403.65) * mm, "mid": v(-385.84, 399.7) * mm, "end": v(-390.1, 391.35) * mm});
            skArc(sketch, "E379", {"start": v(-367.91, 414.4) * mm, "mid": v(-372.37, 412.61) * mm, "end": v(-374.36, 408.24) * mm});
            skArc(sketch, "E380", {"start": v(-357.5, 410.2) * mm, "mid": v(-361.5, 406.2) * mm, "end": v(-357.5, 402.2) * mm});
            skCircle(sketch, "E381", {"center": v(-367.9, 406.2) * mm, "radius": 2.73 * mm});
            skCircle(sketch, "E382", {"center": v(-383.8, 365.65) * mm, "radius": 2.73 * mm});
            skCircle(sketch, "E383", {"center": v(-409.5, 330.22) * mm, "radius": 3 * mm});
            skArc(sketch, "E384", {"start": v(-396.03, 355.34) * mm, "mid": v(-395.29, 356.06) * mm, "end": v(-394.92, 357.03) * mm});
            skArc(sketch, "E385", {"start": v(-377.34, 403.65) * mm, "mid": v(-376.1, 404.16) * mm, "end": v(-375.35, 405.25) * mm});
            skArc(sketch, "E386", {"start": v(-355.82, 413.75) * mm, "mid": v(-356.57, 414.23) * mm, "end": v(-357.44, 414.4) * mm});
            skArc(sketch, "E387", {"start": v(-354.85, 410.2) * mm, "mid": v(-353.47, 410.17) * mm, "end": v(-353.5, 411.55) * mm});
            skArc(sketch, "E388", {"start": v(-374.83, 406.82) * mm, "mid": v(-374.12, 407.37) * mm, "end": v(-374.36, 408.24) * mm});
            skCircle(sketch, "E389", {"center": v(-290.5, 230.52) * mm, "radius": 5 * mm});
            skArc(sketch, "E390", {"start": v(-283.36, 217) * mm, "mid": v(-280.98, 217.98) * mm, "end": v(-280, 220.36) * mm});
            skArc(sketch, "E391", {"start": v(-291.57, 294.28) * mm, "mid": v(-291.88, 293.64) * mm, "end": v(-291.99, 292.94) * mm});
            skArc(sketch, "E392", {"start": v(-291.99, 268.87) * mm, "mid": v(-291.88, 268.16) * mm, "end": v(-291.57, 267.53) * mm});
            skArc(sketch, "E393", {"start": v(-309.9, 391.35) * mm, "mid": v(-314.16, 399.7) * mm, "end": v(-322.66, 403.65) * mm});
            skArc(sketch, "E394", {"start": v(-325.64, 408.24) * mm, "mid": v(-327.63, 412.61) * mm, "end": v(-332.09, 414.4) * mm});
            skArc(sketch, "E395", {"start": v(-342.5, 402.2) * mm, "mid": v(-338.5, 406.2) * mm, "end": v(-342.5, 410.2) * mm});
            skCircle(sketch, "E396", {"center": v(-332.1, 406.2) * mm, "radius": 2.73 * mm});
            skCircle(sketch, "E397", {"center": v(-316.2, 365.65) * mm, "radius": 2.73 * mm});
            skCircle(sketch, "E398", {"center": v(-290.5, 330.22) * mm, "radius": 3 * mm});
            skArc(sketch, "E399", {"start": v(-305.08, 357.03) * mm, "mid": v(-304.71, 356.06) * mm, "end": v(-303.97, 355.34) * mm});
            skArc(sketch, "E400", {"start": v(-324.65, 405.25) * mm, "mid": v(-323.9, 404.16) * mm, "end": v(-322.66, 403.65) * mm});
            skArc(sketch, "E401", {"start": v(-342.56, 414.4) * mm, "mid": v(-343.43, 414.23) * mm, "end": v(-344.18, 413.75) * mm});
            skArc(sketch, "E402", {"start": v(-346.5, 411.55) * mm, "mid": v(-346.53, 410.17) * mm, "end": v(-345.15, 410.2) * mm});
            skArc(sketch, "E403", {"start": v(-325.64, 408.24) * mm, "mid": v(-325.88, 407.37) * mm, "end": v(-325.17, 406.82) * mm});
            skCircle(sketch, "E404", {"center": v(-373.57, 347.4) * mm, "radius": 2.54 * mm});
            skCircle(sketch, "E405", {"center": v(-373.57, 394.54) * mm, "radius": 2.54 * mm});
            skCircle(sketch, "E406", {"center": v(-350, 371.47) * mm, "radius": 12.5 * mm});
            skCircle(sketch, "E407", {"center": v(-326.43, 394.54) * mm, "radius": 2.54 * mm});
            skCircle(sketch, "E408", {"center": v(-326.43, 347.4) * mm, "radius": 2.54 * mm});
            skCircle(sketch, "E409", {"center": v(-380, 230.52) * mm, "radius": 2.5 * mm});
            skCircle(sketch, "E410", {"center": v(-360, 230.52) * mm, "radius": 2.5 * mm});
            skCircle(sketch, "E411", {"center": v(-340, 230.52) * mm, "radius": 2.5 * mm});
            skCircle(sketch, "E412", {"center": v(-320, 230.52) * mm, "radius": 2.5 * mm});
            skCircle(sketch, "E413", {"center": v(-350, 230.52) * mm, "radius": 2.5 * mm});
            skCircle(sketch, "E414", {"center": v(-380, 330.22) * mm, "radius": 2.5 * mm});
            skCircle(sketch, "E415", {"center": v(-360, 330.22) * mm, "radius": 2.5 * mm});
            skCircle(sketch, "E416", {"center": v(-340, 330.22) * mm, "radius": 2.5 * mm});
            skCircle(sketch, "E417", {"center": v(-320, 330.22) * mm, "radius": 2.5 * mm});
            skCircle(sketch, "E418", {"center": v(-350, 330.22) * mm, "radius": 2.5 * mm});
            skCircle(sketch, "E419", {"center": v(-362.46, 314.3) * mm, "radius": 3 * mm});
            skCircle(sketch, "E420", {"center": v(-337.46, 314.3) * mm, "radius": 3 * mm});
            skLineSegment(sketch, "E421", {"start": v(-415.76, 343.34) * mm, "end": v(-414.88, 344.02) * mm});
            skSolve(sketch);
        }
        {
            var Q0;
            Q0 = qSketchRegion(id + "F8", true);
            extrude(context, id + "F9", {"entities" : qUnion([Q0]), "depth" : 3 * mm, "offsetDistance" : 25 * mm});
        }
        {
            var Q0;
            Q0=qCreatedBy(makeId("Top.planeOp"),FACE);
            var sketch = newSketch(context, id + "F10", { "sketchPlane" : qUnion([Q0])});
            skCircle(sketch, "E422", {"center": v(-558, 233.66) * mm, "radius": 2.5 * mm});
            skCircle(sketch, "E423", {"center": v(-538, 233.66) * mm, "radius": 2.5 * mm});
            skCircle(sketch, "E424", {"center": v(-518, 233.66) * mm, "radius": 2.5 * mm});
            skCircle(sketch, "E425", {"center": v(-498, 233.66) * mm, "radius": 2.5 * mm});
            skCircle(sketch, "E426", {"center": v(-528, 233.66) * mm, "radius": 2.5 * mm});
            skCircle(sketch, "E427", {"center": v(-558, 333.36) * mm, "radius": 2.5 * mm});
            skCircle(sketch, "E428", {"center": v(-538, 333.36) * mm, "radius": 2.5 * mm});
            skCircle(sketch, "E429", {"center": v(-518, 333.36) * mm, "radius": 2.5 * mm});
            skCircle(sketch, "E430", {"center": v(-498, 333.36) * mm, "radius": 2.5 * mm});
            skCircle(sketch, "E431", {"center": v(-528, 333.36) * mm, "radius": 2.5 * mm});
            skLineSegment(sketch, "E432", {"start": v(-591.59, 376.34) * mm, "end": v(-573.13, 387.52) * mm});
            skLineSegment(sketch, "E433", {"start": v(-598, 256.25) * mm, "end": v(-598, 228.5) * mm});
            skLineSegment(sketch, "E434", {"start": v(-597.52, 322.45) * mm, "end": v(-591.59, 376.34) * mm});
            skLineSegment(sketch, "E435", {"start": v(-598, 256.25) * mm, "end": v(-597.87, 257.63) * mm});
            skLineSegment(sketch, "E436", {"start": v(-597.87, 257.63) * mm, "end": v(-597.45, 259.12) * mm});
            skLineSegment(sketch, "E437", {"start": v(-597.45, 259.12) * mm, "end": v(-596.74, 260.68) * mm});
            skLineSegment(sketch, "E438", {"start": v(-596.74, 260.68) * mm, "end": v(-595.73, 262.3) * mm});
            skLineSegment(sketch, "E439", {"start": v(-594.64, 225.14) * mm, "end": v(-548.35, 225.14) * mm});
            skLineSegment(sketch, "E440", {"start": v(-507.65, 225.14) * mm, "end": v(-461.36, 225.14) * mm});
            skLineSegment(sketch, "E441", {"start": v(-586, 277) * mm, "end": v(-586, 301.08) * mm});
            skLineSegment(sketch, "E442", {"start": v(-586.43, 302.42) * mm, "end": v(-594.79, 314.4) * mm});
            skLineSegment(sketch, "E443", {"start": v(-594.79, 314.4) * mm, "end": v(-595.92, 316.2) * mm});
            skLineSegment(sketch, "E444", {"start": v(-595.92, 316.2) * mm, "end": v(-596.77, 317.92) * mm});
            skLineSegment(sketch, "E445", {"start": v(-596.77, 317.92) * mm, "end": v(-597.32, 319.55) * mm});
            skLineSegment(sketch, "E446", {"start": v(-597.32, 319.55) * mm, "end": v(-597.57, 321.07) * mm});
            skLineSegment(sketch, "E447", {"start": v(-597.57, 321.07) * mm, "end": v(-597.52, 322.45) * mm});
            skLineSegment(sketch, "E448", {"start": v(-595.73, 262.3) * mm, "end": v(-586.43, 275.66) * mm});
            skLineSegment(sketch, "E449", {"start": v(-522.34, 376.25) * mm, "end": v(-509.16, 387.31) * mm});
            skLineSegment(sketch, "E450", {"start": v(-546.84, 387.31) * mm, "end": v(-533.66, 376.25) * mm});
            skLineSegment(sketch, "E451", {"start": v(-469.57, 275.67) * mm, "end": v(-460.27, 262.3) * mm});
            skLineSegment(sketch, "E452", {"start": v(-461.22, 314.4) * mm, "end": v(-469.57, 302.42) * mm});
            skLineSegment(sketch, "E453", {"start": v(-532.14, 375.7) * mm, "end": v(-523.86, 375.7) * mm});
            skLineSegment(sketch, "E454", {"start": v(-469.99, 301.08) * mm, "end": v(-469.99, 277) * mm});
            skLineSegment(sketch, "E455", {"start": v(-484.09, 387.86) * mm, "end": v(-507.65, 387.86) * mm});
            skLineSegment(sketch, "E456", {"start": v(-548.35, 387.86) * mm, "end": v(-571.91, 387.86) * mm});
            skLineSegment(sketch, "E457", {"start": v(-458, 256.25) * mm, "end": v(-458.13, 257.63) * mm});
            skLineSegment(sketch, "E458", {"start": v(-458.13, 257.63) * mm, "end": v(-458.55, 259.12) * mm});
            skLineSegment(sketch, "E459", {"start": v(-458.55, 259.12) * mm, "end": v(-459.26, 260.68) * mm});
            skLineSegment(sketch, "E460", {"start": v(-459.26, 260.68) * mm, "end": v(-460.27, 262.3) * mm});
            skLineSegment(sketch, "E461", {"start": v(-458.48, 322.45) * mm, "end": v(-458.43, 321.07) * mm});
            skLineSegment(sketch, "E462", {"start": v(-458.43, 321.07) * mm, "end": v(-458.68, 319.55) * mm});
            skLineSegment(sketch, "E463", {"start": v(-458.68, 319.55) * mm, "end": v(-459.23, 317.92) * mm});
            skLineSegment(sketch, "E464", {"start": v(-459.23, 317.92) * mm, "end": v(-460.08, 316.2) * mm});
            skLineSegment(sketch, "E465", {"start": v(-460.08, 316.2) * mm, "end": v(-461.22, 314.4) * mm});
            skLineSegment(sketch, "E466", {"start": v(-458, 228.5) * mm, "end": v(-458, 256.25) * mm});
            skLineSegment(sketch, "E467", {"start": v(-464.41, 376.34) * mm, "end": v(-458.48, 322.45) * mm});
            skLineSegment(sketch, "E468", {"start": v(-482.87, 387.52) * mm, "end": v(-464.41, 376.34) * mm});
            skCircle(sketch, "E469", {"center": v(-587.5, 233.66) * mm, "radius": 5 * mm});
            skArc(sketch, "E470", {"start": v(-598, 228.5) * mm, "mid": v(-597.02, 226.12) * mm, "end": v(-594.64, 225.14) * mm});
            skCircle(sketch, "E471", {"center": v(-538, 289.04) * mm, "radius": 2.5 * mm});
            skCircle(sketch, "E472", {"center": v(-577.85, 252.82) * mm, "radius": 3 * mm});
            skCircle(sketch, "E473", {"center": v(-577.85, 286.14) * mm, "radius": 3 * mm});
            skArc(sketch, "E474", {"start": v(-586.43, 275.66) * mm, "mid": v(-586.11, 276.3) * mm, "end": v(-586, 277) * mm});
            skCircle(sketch, "E475", {"center": v(-577.85, 318.46) * mm, "radius": 3 * mm});
            skCircle(sketch, "E476", {"center": v(-577.85, 368.46) * mm, "radius": 3 * mm});
            skCircle(sketch, "E477", {"center": v(-587.5, 333.36) * mm, "radius": 3 * mm});
            skArc(sketch, "E478", {"start": v(-586, 301.08) * mm, "mid": v(-586.11, 301.78) * mm, "end": v(-586.43, 302.42) * mm});
            skArc(sketch, "E479", {"start": v(-533.66, 376.25) * mm, "mid": v(-532.95, 375.84) * mm, "end": v(-532.14, 375.7) * mm});
            skArc(sketch, "E480", {"start": v(-546.84, 387.31) * mm, "mid": v(-547.54, 387.72) * mm, "end": v(-548.35, 387.86) * mm});
            skArc(sketch, "E481", {"start": v(-571.91, 387.86) * mm, "mid": v(-572.54, 387.77) * mm, "end": v(-573.13, 387.52) * mm});
            skCircle(sketch, "E482", {"center": v(-478.15, 252.82) * mm, "radius": 5 * mm});
            skCircle(sketch, "E483", {"center": v(-478.15, 286.14) * mm, "radius": 5 * mm});
            skCircle(sketch, "E484", {"center": v(-468.5, 233.66) * mm, "radius": 5 * mm});
            skArc(sketch, "E485", {"start": v(-461.36, 225.14) * mm, "mid": v(-458.98, 226.12) * mm, "end": v(-458, 228.5) * mm});
            skCircle(sketch, "E486", {"center": v(-518, 289.04) * mm, "radius": 2.5 * mm});
            skArc(sketch, "E487", {"start": v(-469.99, 277) * mm, "mid": v(-469.88, 276.3) * mm, "end": v(-469.57, 275.67) * mm});
            skCircle(sketch, "E488", {"center": v(-478.15, 318.46) * mm, "radius": 5 * mm});
            skCircle(sketch, "E489", {"center": v(-478.15, 368.46) * mm, "radius": 5 * mm});
            skCircle(sketch, "E490", {"center": v(-468.5, 333.36) * mm, "radius": 3 * mm});
            skArc(sketch, "E491", {"start": v(-469.57, 302.42) * mm, "mid": v(-469.88, 301.78) * mm, "end": v(-469.99, 301.08) * mm});
            skArc(sketch, "E492", {"start": v(-523.86, 375.7) * mm, "mid": v(-523.05, 375.84) * mm, "end": v(-522.34, 376.25) * mm});
            skArc(sketch, "E493", {"start": v(-507.65, 387.86) * mm, "mid": v(-508.46, 387.72) * mm, "end": v(-509.16, 387.31) * mm});
            skArc(sketch, "E494", {"start": v(-482.87, 387.52) * mm, "mid": v(-483.46, 387.77) * mm, "end": v(-484.09, 387.86) * mm});
            skLineSegment(sketch, "E495", {"start": v(-548.35, 225.14) * mm, "end": v(-507.65, 225.14) * mm});
            skSolve(sketch);
        }
        {
            var Q0;
            Q0 = qSketchRegion(id + "F10", true);
            extrude(context, id + "F11", {"entities" : qUnion([Q0]), "depth" : 3 * mm, "offsetDistance" : 25 * mm});
        }
        {
            var Q0;
            Q0=qCreatedBy(makeId("Top.planeOp"),FACE);
            var sketch = newSketch(context, id + "F12", { "sketchPlane" : qUnion([Q0])});
            skCircle(sketch, "E496", {"center": v(-725, 517.6) * mm, "radius": 2.5 * mm});
            skCircle(sketch, "E497", {"center": v(-705, 517.6) * mm, "radius": 2.5 * mm});
            skCircle(sketch, "E498", {"center": v(-685, 517.6) * mm, "radius": 2.5 * mm});
            skCircle(sketch, "E499", {"center": v(-665, 517.6) * mm, "radius": 2.5 * mm});
            skCircle(sketch, "E500", {"center": v(-695, 517.6) * mm, "radius": 2.5 * mm});
            skCircle(sketch, "E501", {"center": v(-725, 617.3) * mm, "radius": 2.5 * mm});
            skCircle(sketch, "E502", {"center": v(-705, 617.3) * mm, "radius": 2.5 * mm});
            skCircle(sketch, "E503", {"center": v(-685, 617.3) * mm, "radius": 2.5 * mm});
            skCircle(sketch, "E504", {"center": v(-665, 617.3) * mm, "radius": 2.5 * mm});
            skCircle(sketch, "E505", {"center": v(-695, 617.3) * mm, "radius": 2.5 * mm});
            skLineSegment(sketch, "E506", {"start": v(-768, 507.6) * mm, "end": v(-715.35, 507.6) * mm});
            skLineSegment(sketch, "E507", {"start": v(-773, 512.6) * mm, "end": v(-773, 641.8) * mm});
            skLineSegment(sketch, "E508", {"start": v(-689.34, 635.2) * mm, "end": v(-676.16, 646.25) * mm});
            skLineSegment(sketch, "E509", {"start": v(-713.84, 646.25) * mm, "end": v(-700.66, 635.2) * mm});
            skLineSegment(sketch, "E510", {"start": v(-699.14, 634.64) * mm, "end": v(-690.86, 634.64) * mm});
            skLineSegment(sketch, "E511", {"start": v(-715.35, 646.8) * mm, "end": v(-768, 646.8) * mm});
            skCircle(sketch, "E512", {"center": v(-705, 572.98) * mm, "radius": 2.5 * mm});
            skArc(sketch, "E513", {"start": v(-700.66, 635.2) * mm, "mid": v(-699.95, 634.78) * mm, "end": v(-699.14, 634.64) * mm});
            skArc(sketch, "E514", {"start": v(-713.84, 646.25) * mm, "mid": v(-714.54, 646.66) * mm, "end": v(-715.35, 646.8) * mm});
            skCircle(sketch, "E515", {"center": v(-685, 572.98) * mm, "radius": 2.5 * mm});
            skArc(sketch, "E516", {"start": v(-690.86, 634.64) * mm, "mid": v(-690.05, 634.78) * mm, "end": v(-689.34, 635.2) * mm});
            skArc(sketch, "E517", {"start": v(-674.65, 646.8) * mm, "mid": v(-675.46, 646.66) * mm, "end": v(-676.16, 646.25) * mm});
            skLineSegment(sketch, "E518", {"start": v(-715.35, 507.6) * mm, "end": v(-674.65, 507.6) * mm});
            skCircle(sketch, "E519", {"center": v(-749.5, 517.6) * mm, "radius": 5 * mm});
            skCircle(sketch, "E520", {"center": v(-751.5, 617.3) * mm, "radius": 3 * mm});
            skLineSegment(sketch, "E521", {"start": v(-773, 641.8) * mm, "end": v(-768, 646.8) * mm});
            skLineSegment(sketch, "E522", {"start": v(-773, 512.6) * mm, "end": v(-768, 507.6) * mm});
            skCircle(sketch, "E523", {"center": v(-640.5, 517.6) * mm, "radius": 5 * mm});
            skCircle(sketch, "E524", {"center": v(-638.5, 617.3) * mm, "radius": 3 * mm});
            skLineSegment(sketch, "E525", {"start": v(-617, 641.8) * mm, "end": v(-622, 646.8) * mm});
            skLineSegment(sketch, "E526", {"start": v(-617, 512.6) * mm, "end": v(-622, 507.6) * mm});
            skLineSegment(sketch, "E527", {"start": v(-617, 512.6) * mm, "end": v(-617, 641.8) * mm});
            skLineSegment(sketch, "E528", {"start": v(-622, 507.6) * mm, "end": v(-674.65, 507.6) * mm});
            skLineSegment(sketch, "E529", {"start": v(-674.65, 646.8) * mm, "end": v(-622, 646.8) * mm});
            skCircle(sketch, "E530", {"center": v(-762, 537.6) * mm, "radius": 3 * mm});
            skCircle(sketch, "E531", {"center": v(-722, 537.6) * mm, "radius": 3 * mm});
            skCircle(sketch, "E532", {"center": v(-762, 577.6) * mm, "radius": 3 * mm});
            skCircle(sketch, "E533", {"center": v(-722, 577.6) * mm, "radius": 3 * mm});
            skCircle(sketch, "E534", {"center": v(-762, 637.3) * mm, "radius": 3 * mm});
            skCircle(sketch, "E535", {"center": v(-722, 637.3) * mm, "radius": 3 * mm});
            skCircle(sketch, "E536", {"center": v(-762, 597.3) * mm, "radius": 3 * mm});
            skCircle(sketch, "E537", {"center": v(-722, 597.3) * mm, "radius": 3 * mm});
            skCircle(sketch, "E538", {"center": v(-628, 637.3) * mm, "radius": 3 * mm});
            skCircle(sketch, "E539", {"center": v(-668, 637.3) * mm, "radius": 3 * mm});
            skCircle(sketch, "E540", {"center": v(-628, 597.3) * mm, "radius": 3 * mm});
            skCircle(sketch, "E541", {"center": v(-668, 597.3) * mm, "radius": 3 * mm});
            skCircle(sketch, "E542", {"center": v(-628, 537.6) * mm, "radius": 3 * mm});
            skCircle(sketch, "E543", {"center": v(-668, 537.6) * mm, "radius": 3 * mm});
            skCircle(sketch, "E544", {"center": v(-628, 577.6) * mm, "radius": 3 * mm});
            skCircle(sketch, "E545", {"center": v(-668, 577.6) * mm, "radius": 3 * mm});
            skSolve(sketch);
        }
        {
            var Q0;
            Q0 = qSketchRegion(id + "F12", true);
            extrude(context, id + "F13", {"entities" : qUnion([Q0]), "depth" : 3 * mm, "offsetDistance" : 25 * mm});
        }
        {
            var Q0;
            Q0=qCreatedBy(makeId("Top.planeOp"),FACE);
            var sketch = newSketch(context, id + "F14", { "sketchPlane" : qUnion([Q0])});
            skCircle(sketch, "E546", {"center": v(-543, 516.4) * mm, "radius": 2.5 * mm});
            skCircle(sketch, "E547", {"center": v(-523, 516.4) * mm, "radius": 2.5 * mm});
            skCircle(sketch, "E548", {"center": v(-503, 516.4) * mm, "radius": 2.5 * mm});
            skCircle(sketch, "E549", {"center": v(-483, 516.4) * mm, "radius": 2.5 * mm});
            skCircle(sketch, "E550", {"center": v(-513, 516.4) * mm, "radius": 2.5 * mm});
            skCircle(sketch, "E551", {"center": v(-543, 636.1) * mm, "radius": 2.5 * mm});
            skCircle(sketch, "E552", {"center": v(-523, 636.1) * mm, "radius": 2.5 * mm});
            skCircle(sketch, "E553", {"center": v(-503, 636.1) * mm, "radius": 2.5 * mm});
            skCircle(sketch, "E554", {"center": v(-483, 636.1) * mm, "radius": 2.5 * mm});
            skCircle(sketch, "E555", {"center": v(-513, 636.1) * mm, "radius": 2.5 * mm});
            skLineSegment(sketch, "E556", {"start": v(-581, 506.4) * mm, "end": v(-533.35, 506.4) * mm});
            skLineSegment(sketch, "E557", {"start": v(-586, 511.4) * mm, "end": v(-586, 650.6) * mm});
            skLineSegment(sketch, "E558", {"start": v(-492.65, 655.6) * mm, "end": v(-581, 655.6) * mm});
            skCircle(sketch, "E559", {"center": v(-523, 577.78) * mm, "radius": 2.5 * mm});
            skCircle(sketch, "E560", {"center": v(-503, 577.78) * mm, "radius": 2.5 * mm});
            skLineSegment(sketch, "E561", {"start": v(-533.35, 506.4) * mm, "end": v(-492.65, 506.4) * mm});
            skCircle(sketch, "E562", {"center": v(-572.5, 516.4) * mm, "radius": 5 * mm});
            skCircle(sketch, "E563", {"center": v(-574.5, 636.1) * mm, "radius": 3 * mm});
            skLineSegment(sketch, "E564", {"start": v(-586, 650.6) * mm, "end": v(-581, 655.6) * mm});
            skLineSegment(sketch, "E565", {"start": v(-586, 511.4) * mm, "end": v(-581, 506.4) * mm});
            skCircle(sketch, "E566", {"center": v(-453.5, 516.4) * mm, "radius": 5 * mm});
            skCircle(sketch, "E567", {"center": v(-451.5, 636.1) * mm, "radius": 3 * mm});
            skLineSegment(sketch, "E568", {"start": v(-440, 650.6) * mm, "end": v(-445, 655.6) * mm});
            skLineSegment(sketch, "E569", {"start": v(-440, 511.4) * mm, "end": v(-445, 506.4) * mm});
            skLineSegment(sketch, "E570", {"start": v(-440, 511.4) * mm, "end": v(-440, 650.6) * mm});
            skLineSegment(sketch, "E571", {"start": v(-445, 506.4) * mm, "end": v(-492.65, 506.4) * mm});
            skLineSegment(sketch, "E572", {"start": v(-492.65, 655.6) * mm, "end": v(-445, 655.6) * mm});
            skCircle(sketch, "E573", {"center": v(-580, 625.1) * mm, "radius": 3 * mm});
            skCircle(sketch, "E574", {"center": v(-540, 625.1) * mm, "radius": 3 * mm});
            skCircle(sketch, "E575", {"center": v(-580, 585.1) * mm, "radius": 3 * mm});
            skCircle(sketch, "E576", {"center": v(-540, 585.1) * mm, "radius": 3 * mm});
            skCircle(sketch, "E577", {"center": v(-580, 530.46) * mm, "radius": 3 * mm});
            skCircle(sketch, "E578", {"center": v(-540, 530.46) * mm, "radius": 3 * mm});
            skCircle(sketch, "E579", {"center": v(-580, 570.46) * mm, "radius": 3 * mm});
            skCircle(sketch, "E580", {"center": v(-540, 570.46) * mm, "radius": 3 * mm});
            skCircle(sketch, "E581", {"center": v(-446, 625.1) * mm, "radius": 3 * mm});
            skCircle(sketch, "E582", {"center": v(-486, 625.1) * mm, "radius": 3 * mm});
            skCircle(sketch, "E583", {"center": v(-446, 585.1) * mm, "radius": 3 * mm});
            skCircle(sketch, "E584", {"center": v(-486, 585.1) * mm, "radius": 3 * mm});
            skCircle(sketch, "E585", {"center": v(-446, 530.46) * mm, "radius": 3 * mm});
            skCircle(sketch, "E586", {"center": v(-486, 530.46) * mm, "radius": 3 * mm});
            skCircle(sketch, "E587", {"center": v(-446, 570.46) * mm, "radius": 3 * mm});
            skCircle(sketch, "E588", {"center": v(-486, 570.46) * mm, "radius": 3 * mm});
            skSolve(sketch);
        }
        {
            var Q0;
            Q0 = qSketchRegion(id + "F14", true);
            extrude(context, id + "F15", {"entities" : qUnion([Q0]), "depth" : 3 * mm, "offsetDistance" : 25 * mm});
        }
        {
            var Q0;
            Q0=qCreatedBy(makeId("Top.planeOp"),FACE);
            var sketch = newSketch(context, id + "F16", { "sketchPlane" : qUnion([Q0])});
            skCircle(sketch, "E589", {"center": v(-227, 514.5) * mm, "radius": 5 * mm});
            skCircle(sketch, "E590", {"center": v(-302, 514.5) * mm, "radius": 5 * mm});
            skCircle(sketch, "E591", {"center": v(-377, 514.5) * mm, "radius": 5 * mm});
            skCircle(sketch, "E592", {"center": v(-227, 614.2) * mm, "radius": 3 * mm});
            skCircle(sketch, "E593", {"center": v(-267, 614.2) * mm, "radius": 3 * mm});
            skCircle(sketch, "E594", {"center": v(-337, 614.2) * mm, "radius": 3 * mm});
            skCircle(sketch, "E595", {"center": v(-377, 614.2) * mm, "radius": 3 * mm});
            skLineSegment(sketch, "E596", {"start": v(-392, 775.61) * mm, "end": v(-392, 647) * mm});
            skArc(sketch, "E597", {"start": v(-382.54, 781) * mm, "mid": v(-387.98, 779.56) * mm, "end": v(-392, 775.61) * mm});
            skLineSegment(sketch, "E598", {"start": v(-223, 781) * mm, "end": v(-382.54, 781) * mm});
            skArc(sketch, "E599", {"start": v(-212, 770) * mm, "mid": v(-215.22, 777.78) * mm, "end": v(-223, 781) * mm});
            skLineSegment(sketch, "E600", {"start": v(-212, 504) * mm, "end": v(-212, 770) * mm});
            skArc(sketch, "E601", {"start": v(-215, 501) * mm, "mid": v(-212.88, 501.88) * mm, "end": v(-212, 504) * mm});
            skLineSegment(sketch, "E602", {"start": v(-389, 501) * mm, "end": v(-215, 501) * mm});
            skArc(sketch, "E603", {"start": v(-392, 504) * mm, "mid": v(-391.12, 501.88) * mm, "end": v(-389, 501) * mm});
            skLineSegment(sketch, "E604", {"start": v(-392, 647) * mm, "end": v(-392, 504) * mm});
            skCircle(sketch, "E605", {"center": v(-348.07, 718.93) * mm, "radius": 2.54 * mm});
            skCircle(sketch, "E606", {"center": v(-348.07, 766.07) * mm, "radius": 2.54 * mm});
            skCircle(sketch, "E607", {"center": v(-324.5, 743) * mm, "radius": 12.5 * mm});
            skCircle(sketch, "E608", {"center": v(-300.93, 766.07) * mm, "radius": 2.54 * mm});
            skCircle(sketch, "E609", {"center": v(-300.93, 718.93) * mm, "radius": 2.54 * mm});
            skCircle(sketch, "E610", {"center": v(-284.5, 763) * mm, "radius": 2.5 * mm});
            skCircle(sketch, "E611", {"center": v(-284.5, 743) * mm, "radius": 2.5 * mm});
            skCircle(sketch, "E612", {"center": v(-284.5, 723) * mm, "radius": 2.5 * mm});
            skCircle(sketch, "E613", {"center": v(-357, 614.2) * mm, "radius": 3 * mm});
            skCircle(sketch, "E614", {"center": v(-247, 614.2) * mm, "radius": 3 * mm});
            skCircle(sketch, "E615", {"center": v(-337, 571.07) * mm, "radius": 3 * mm});
            skCircle(sketch, "E616", {"center": v(-312, 571.07) * mm, "radius": 3 * mm});
            skCircle(sketch, "E617", {"center": v(-294.5, 611.07) * mm, "radius": 3 * mm});
            skCircle(sketch, "E618", {"center": v(-262.5, 603.07) * mm, "radius": 2.5 * mm});
            skCircle(sketch, "E619", {"center": v(-326.5, 603.07) * mm, "radius": 2.5 * mm});
            skCircle(sketch, "E620", {"center": v(-326.5, 539.07) * mm, "radius": 2.5 * mm});
            skCircle(sketch, "E621", {"center": v(-262.5, 539.07) * mm, "radius": 2.5 * mm});
            skCircle(sketch, "E622", {"center": v(-364.5, 763) * mm, "radius": 2.5 * mm});
            skCircle(sketch, "E623", {"center": v(-364.5, 743) * mm, "radius": 2.5 * mm});
            skCircle(sketch, "E624", {"center": v(-364.5, 723) * mm, "radius": 2.5 * mm});
            skCircle(sketch, "E625", {"center": v(-364.5, 703) * mm, "radius": 2.5 * mm});
            skCircle(sketch, "E626", {"center": v(-284.5, 703) * mm, "radius": 2.5 * mm});
            skSolve(sketch);
        }
        {
            var Q0;
            Q0 = qSketchRegion(id + "F16", true);
            extrude(context, id + "F17", {"entities" : qUnion([Q0]), "depth" : 25 * mm, "offsetDistance" : 25 * mm});
        }
        {
            var Q0;
            Q0=qCreatedBy(makeId("Top.planeOp"),FACE);
            var sketch = newSketch(context, id + "F18", { "sketchPlane" : qUnion([Q0])});
            skLineSegment(sketch, "E627", {"start": v(-557.92, 854.94) * mm, "end": v(-553.1, 889.27) * mm});
            skLineSegment(sketch, "E628", {"start": v(-581, 837.63) * mm, "end": v(-557.92, 854.94) * mm});
            skLineSegment(sketch, "E629", {"start": v(-468.08, 854.94) * mm, "end": v(-445, 837.63) * mm});
            skLineSegment(sketch, "E630", {"start": v(-472.9, 889.27) * mm, "end": v(-468.08, 854.94) * mm});
            skArc(sketch, "E631", {"start": v(-540.34, 901.57) * mm, "mid": v(-548.84, 897.61) * mm, "end": v(-553.1, 889.27) * mm});
            skCircle(sketch, "E632", {"center": v(-546.8, 873.56) * mm, "radius": 2.73 * mm});
            skArc(sketch, "E633", {"start": v(-472.9, 889.27) * mm, "mid": v(-477.16, 897.61) * mm, "end": v(-485.66, 901.57) * mm});
            skCircle(sketch, "E634", {"center": v(-479.2, 873.56) * mm, "radius": 2.73 * mm});
            skCircle(sketch, "E635", {"center": v(-536.57, 835.31) * mm, "radius": 2.54 * mm});
            skCircle(sketch, "E636", {"center": v(-536.57, 882.45) * mm, "radius": 2.54 * mm});
            skCircle(sketch, "E637", {"center": v(-513, 859.38) * mm, "radius": 12.5 * mm});
            skCircle(sketch, "E638", {"center": v(-489.43, 882.45) * mm, "radius": 2.54 * mm});
            skCircle(sketch, "E639", {"center": v(-489.43, 835.31) * mm, "radius": 2.54 * mm});
            skCircle(sketch, "E640", {"center": v(-543, 698.43) * mm, "radius": 2.5 * mm});
            skCircle(sketch, "E641", {"center": v(-523, 698.43) * mm, "radius": 2.5 * mm});
            skCircle(sketch, "E642", {"center": v(-503, 698.43) * mm, "radius": 2.5 * mm});
            skCircle(sketch, "E643", {"center": v(-483, 698.43) * mm, "radius": 2.5 * mm});
            skCircle(sketch, "E644", {"center": v(-513, 698.43) * mm, "radius": 2.5 * mm});
            skCircle(sketch, "E645", {"center": v(-543, 818.13) * mm, "radius": 2.5 * mm});
            skCircle(sketch, "E646", {"center": v(-523, 818.13) * mm, "radius": 2.5 * mm});
            skCircle(sketch, "E647", {"center": v(-503, 818.13) * mm, "radius": 2.5 * mm});
            skCircle(sketch, "E648", {"center": v(-483, 818.13) * mm, "radius": 2.5 * mm});
            skCircle(sketch, "E649", {"center": v(-513, 818.13) * mm, "radius": 2.5 * mm});
            skLineSegment(sketch, "E650", {"start": v(-581, 688.43) * mm, "end": v(-533.35, 688.43) * mm});
            skLineSegment(sketch, "E651", {"start": v(-586, 693.43) * mm, "end": v(-586, 832.63) * mm});
            skLineSegment(sketch, "E652", {"start": v(-533.35, 688.43) * mm, "end": v(-492.65, 688.43) * mm});
            skCircle(sketch, "E653", {"center": v(-572.5, 698.43) * mm, "radius": 5 * mm});
            skCircle(sketch, "E654", {"center": v(-574.5, 818.13) * mm, "radius": 3 * mm});
            skLineSegment(sketch, "E655", {"start": v(-586, 832.63) * mm, "end": v(-581, 837.63) * mm});
            skLineSegment(sketch, "E656", {"start": v(-586, 693.43) * mm, "end": v(-581, 688.43) * mm});
            skCircle(sketch, "E657", {"center": v(-453.5, 698.43) * mm, "radius": 5 * mm});
            skCircle(sketch, "E658", {"center": v(-451.5, 818.13) * mm, "radius": 3 * mm});
            skLineSegment(sketch, "E659", {"start": v(-440, 832.63) * mm, "end": v(-445, 837.63) * mm});
            skLineSegment(sketch, "E660", {"start": v(-440, 693.43) * mm, "end": v(-445, 688.43) * mm});
            skLineSegment(sketch, "E661", {"start": v(-440, 693.43) * mm, "end": v(-440, 832.63) * mm});
            skLineSegment(sketch, "E662", {"start": v(-445, 688.43) * mm, "end": v(-492.65, 688.43) * mm});
            skLineSegment(sketch, "E663", {"start": v(-540.34, 901.57) * mm, "end": v(-485.66, 901.57) * mm});
            skSolve(sketch);
        }
        {
            var Q0;
            Q0 = qSketchRegion(id + "F18", true);
            extrude(context, id + "F19", {"entities" : qUnion([Q0]), "depth" : -25 * mm, "offsetDistance" : 25 * mm});
        }
        {
            var Q0;
            Q0=qCreatedBy(makeId("Top.planeOp"),FACE);
            var sketch = newSketch(context, id + "F20", { "sketchPlane" : qUnion([Q0])});
            skCircle(sketch, "E664", {"center": v(-547, 959.95) * mm, "radius": 2.5 * mm});
            skCircle(sketch, "E665", {"center": v(-527, 959.95) * mm, "radius": 2.5 * mm});
            skCircle(sketch, "E666", {"center": v(-507, 959.95) * mm, "radius": 2.5 * mm});
            skCircle(sketch, "E667", {"center": v(-487, 959.95) * mm, "radius": 2.5 * mm});
            skCircle(sketch, "E668", {"center": v(-517, 959.95) * mm, "radius": 2.5 * mm});
            skLineSegment(sketch, "E669", {"start": v(-543.11, 1042.02) * mm, "end": v(-543.11, 1039.02) * mm});
            skLineSegment(sketch, "E670", {"start": v(-543.11, 994.88) * mm, "end": v(-543.11, 991.88) * mm});
            skLineSegment(sketch, "E671", {"start": v(-538.03, 991.88) * mm, "end": v(-538.03, 994.88) * mm});
            skLineSegment(sketch, "E672", {"start": v(-538.03, 1042.02) * mm, "end": v(-538.03, 1039.02) * mm});
            skLineSegment(sketch, "E673", {"start": v(-495.97, 1042.02) * mm, "end": v(-495.97, 1039.02) * mm});
            skLineSegment(sketch, "E674", {"start": v(-490.9, 1042.02) * mm, "end": v(-490.9, 1039.02) * mm});
            skLineSegment(sketch, "E675", {"start": v(-495.97, 994.88) * mm, "end": v(-495.97, 991.88) * mm});
            skLineSegment(sketch, "E676", {"start": v(-490.9, 994.88) * mm, "end": v(-490.9, 991.88) * mm});
            skArc(sketch, "E677", {"start": v(-543.11, 991.88) * mm, "mid": v(-540.57, 989.34) * mm, "end": v(-538.03, 991.88) * mm});
            skArc(sketch, "E678", {"start": v(-543.11, 1039.02) * mm, "mid": v(-540.57, 1036.48) * mm, "end": v(-538.03, 1039.02) * mm});
            skArc(sketch, "E679", {"start": v(-529.5, 1015.95) * mm, "mid": v(-517, 1003.45) * mm, "end": v(-504.5, 1015.95) * mm});
            skArc(sketch, "E680", {"start": v(-495.97, 1039.02) * mm, "mid": v(-493.43, 1036.48) * mm, "end": v(-490.9, 1039.02) * mm});
            skArc(sketch, "E681", {"start": v(-495.97, 991.88) * mm, "mid": v(-493.43, 989.34) * mm, "end": v(-490.9, 991.88) * mm});
            skArc(sketch, "E682", {"start": v(-538.03, 994.88) * mm, "mid": v(-540.57, 997.42) * mm, "end": v(-543.11, 994.88) * mm});
            skArc(sketch, "E683", {"start": v(-538.03, 1042.02) * mm, "mid": v(-540.57, 1044.56) * mm, "end": v(-543.11, 1042.02) * mm});
            skArc(sketch, "E684", {"start": v(-504.5, 1018.95) * mm, "mid": v(-517, 1031.45) * mm, "end": v(-529.5, 1018.95) * mm});
            skArc(sketch, "E685", {"start": v(-490.9, 1042.02) * mm, "mid": v(-493.43, 1044.56) * mm, "end": v(-495.97, 1042.02) * mm});
            skArc(sketch, "E686", {"start": v(-490.9, 994.88) * mm, "mid": v(-493.43, 997.42) * mm, "end": v(-495.97, 994.88) * mm});
            skLineSegment(sketch, "E687", {"start": v(-529.5, 1018.95) * mm, "end": v(-529.5, 1015.95) * mm});
            skLineSegment(sketch, "E688", {"start": v(-504.5, 1018.95) * mm, "end": v(-504.5, 1015.95) * mm});
            skCircle(sketch, "E689", {"center": v(-552, 981.67) * mm, "radius": 3.5 * mm});
            skCircle(sketch, "E690", {"center": v(-576, 1023.24) * mm, "radius": 3.5 * mm});
            skCircle(sketch, "E691", {"center": v(-564, 1002.45) * mm, "radius": 10 * mm});
            skCircle(sketch, "E692", {"center": v(-482, 981.67) * mm, "radius": 3.5 * mm});
            skCircle(sketch, "E693", {"center": v(-458, 1023.24) * mm, "radius": 3.5 * mm});
            skCircle(sketch, "E694", {"center": v(-470, 1002.45) * mm, "radius": 10 * mm});
            skLineSegment(sketch, "E695", {"start": v(-586.58, 1018.48) * mm, "end": v(-554.5, 950.95) * mm});
            skLineSegment(sketch, "E696", {"start": v(-554.5, 950.95) * mm, "end": v(-479.5, 950.95) * mm});
            skLineSegment(sketch, "E697", {"start": v(-479.5, 950.95) * mm, "end": v(-447.42, 1018.48) * mm});
            skLineSegment(sketch, "E698", {"start": v(-452.08, 1032.25) * mm, "end": v(-487.54, 1051.05) * mm});
            skLineSegment(sketch, "E699", {"start": v(-487.54, 1051.05) * mm, "end": v(-546.46, 1051.05) * mm});
            skLineSegment(sketch, "E700", {"start": v(-546.46, 1051.05) * mm, "end": v(-581.92, 1032.25) * mm});
            skLineSegment(sketch, "E701", {"start": v(-586.58, 1018.48) * mm, "end": v(-581.92, 1032.25) * mm});
            skLineSegment(sketch, "E702", {"start": v(-452.08, 1032.25) * mm, "end": v(-447.42, 1018.48) * mm});
            skCircle(sketch, "E703", {"center": v(-537, 959.95) * mm, "radius": 2.5 * mm});
            skCircle(sketch, "E704", {"center": v(-497, 959.95) * mm, "radius": 2.5 * mm});
            skSolve(sketch);
        }
        {
            var Q0;
            Q0 = qSketchRegion(id + "F20", true);
            extrude(context, id + "F21", {"entities" : qUnion([Q0]), "depth" : 3 * mm, "offsetDistance" : 25 * mm});
        }
        {
            var Q0;
            Q0=qCreatedBy(makeId("Top.planeOp"),FACE);
            var sketch = newSketch(context, id + "F22", { "sketchPlane" : qUnion([Q0])});
            skCircle(sketch, "E705", {"center": v(-765.25, 799.5) * mm, "radius": 2.5 * mm});
            skCircle(sketch, "E706", {"center": v(-765.25, 779.5) * mm, "radius": 2.5 * mm});
            skCircle(sketch, "E707", {"center": v(-765.25, 759.5) * mm, "radius": 2.5 * mm});
            skCircle(sketch, "E708", {"center": v(-765.25, 739.5) * mm, "radius": 2.5 * mm});
            skCircle(sketch, "E709", {"center": v(-735.25, 739.5) * mm, "radius": 2.5 * mm});
            skCircle(sketch, "E710", {"center": v(-705.25, 739.5) * mm, "radius": 2.5 * mm});
            skCircle(sketch, "E711", {"center": v(-765.25, 719.5) * mm, "radius": 2.5 * mm});
            skCircle(sketch, "E712", {"center": v(-735.25, 719.5) * mm, "radius": 2.5 * mm});
            skCircle(sketch, "E713", {"center": v(-705.25, 719.5) * mm, "radius": 2.5 * mm});
            skArc(sketch, "E714", {"start": v(-755.25, 799.5) * mm, "mid": v(-758.18, 806.57) * mm, "end": v(-765.25, 809.5) * mm});
            skArc(sketch, "E715", {"start": v(-696.25, 739.5) * mm, "mid": v(-698.89, 745.86) * mm, "end": v(-705.25, 748.5) * mm});
            skArc(sketch, "E716", {"start": v(-705.25, 710.5) * mm, "mid": v(-698.89, 713.14) * mm, "end": v(-696.25, 719.5) * mm});
            skLineSegment(sketch, "E717", {"start": v(-696.25, 739.5) * mm, "end": v(-696.25, 719.5) * mm});
            skLineSegment(sketch, "E718", {"start": v(-705.25, 748.5) * mm, "end": v(-755.25, 748.5) * mm});
            skLineSegment(sketch, "E719", {"start": v(-705.25, 710.5) * mm, "end": v(-776.3, 710.5) * mm});
            skLineSegment(sketch, "E720", {"start": v(-755.25, 799.5) * mm, "end": v(-755.25, 748.5) * mm});
            skCircle(sketch, "E721", {"center": v(-796.75, 779.5) * mm, "radius": 3 * mm});
            skCircle(sketch, "E722", {"center": v(-841.75, 779.5) * mm, "radius": 3 * mm});
            skArc(sketch, "E723", {"start": v(-861.75, 779.5) * mm, "mid": v(-855.9, 765.36) * mm, "end": v(-841.75, 759.5) * mm});
            skLineSegment(sketch, "E724", {"start": v(-861.75, 779.5) * mm, "end": v(-861.75, 809.5) * mm});
            skLineSegment(sketch, "E725", {"start": v(-841.75, 759.5) * mm, "end": v(-776.3, 710.5) * mm});
            skLineSegment(sketch, "E726", {"start": v(-861.75, 809.5) * mm, "end": v(-765.25, 809.5) * mm});
            skSolve(sketch);
        }
        {
            var Q0;
            Q0 = qSketchRegion(id + "F22", true);
            extrude(context, id + "F23", {"entities" : qUnion([Q0]), "depth" : 25 * mm, "offsetDistance" : 25 * mm});
        }
    });
